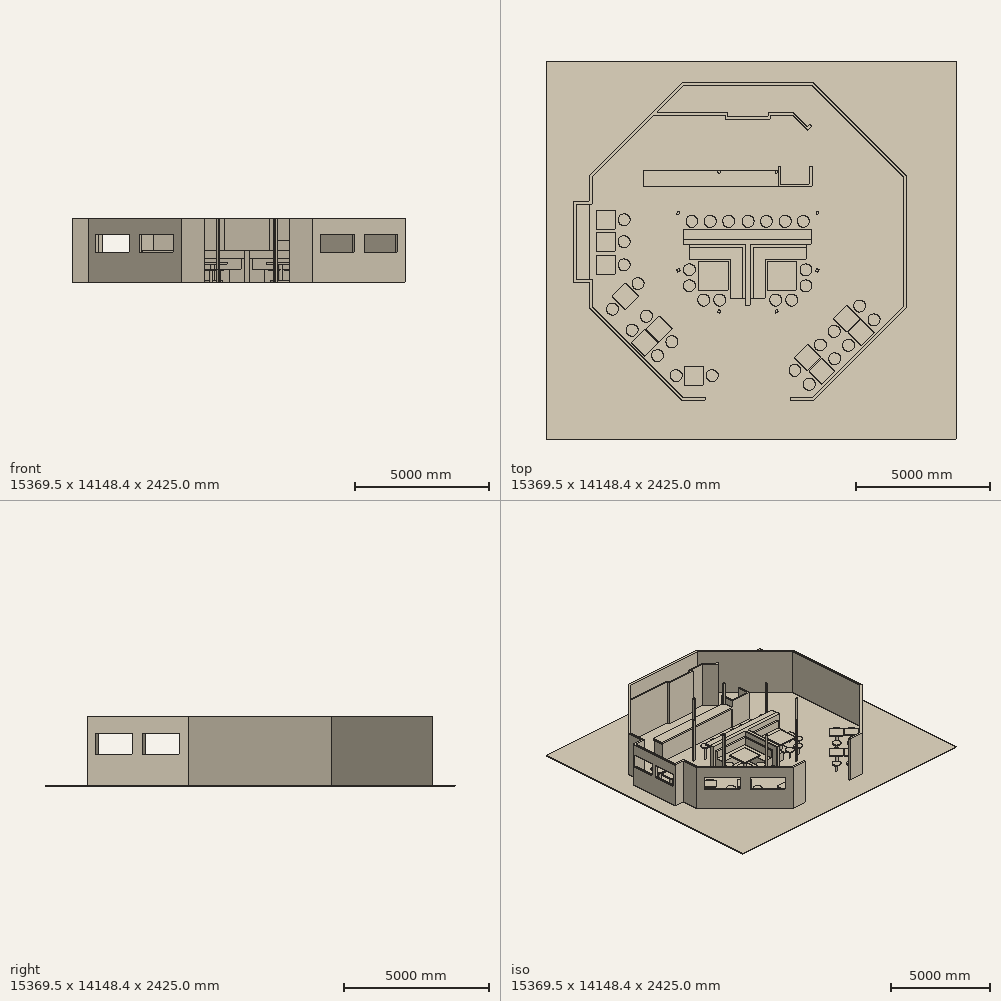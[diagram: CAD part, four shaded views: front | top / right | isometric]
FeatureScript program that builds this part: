
annotation { "Feature Type Name" : "Feature", "Feature Type Description" : "" }
export const myFeature = defineFeature(function(context is Context, id is Id, definition is map)
    precondition{}
    {
        {
            var Q0;
            Q0=qCreatedBy(makeId("Top.planeOp"),FACE);
            var sketch = newSketch(context, id + "F0", { "sketchPlane" : qUnion([Q0])});
            skLineSegment(sketch, "E0", {"start": v(-3956.26, -4309.82) * mm, "end": v(-4034.04, -4387.6) * mm});
            skLineSegment(sketch, "E1", {"start": v(-4309.82, -3956.26) * mm, "end": v(-4387.6, -4034.04) * mm});
            skLineSegment(sketch, "E2", {"start": v(-5582.6, -2683.47) * mm, "end": v(-5660.39, -2761.25) * mm});
            skLineSegment(sketch, "E3", {"start": v(-2683.47, -5582.6) * mm, "end": v(-2761.25, -5660.39) * mm});
            skLineSegment(sketch, "E4", {"start": v(-5845, -1400) * mm, "end": v(-6555, -1400) * mm});
            skLineSegment(sketch, "E5", {"start": v(-6445, 1400) * mm, "end": v(-6445, -1400) * mm});
            skLineSegment(sketch, "E6", {"start": v(-6555, 1510) * mm, "end": v(-6555, -1510) * mm});
            skLineSegment(sketch, "E7", {"start": v(-5955, -1510) * mm, "end": v(-6555, -1510) * mm});
            skLineSegment(sketch, "E8", {"start": v(-5845, 1400) * mm, "end": v(-6555, 1400) * mm});
            skLineSegment(sketch, "E9", {"start": v(-5955, 1510) * mm, "end": v(-6555, 1510) * mm});
            skLineSegment(sketch, "E10", {"start": v(-5845, -2421.08) * mm, "end": v(-2421.08, -5845) * mm});
            skLineSegment(sketch, "E11", {"start": v(-2421.08, -5845) * mm, "end": v(2421.08, -5845) * mm});
            skLineSegment(sketch, "E12", {"start": v(2421.08, -5845) * mm, "end": v(5845, -2421.08) * mm});
            skLineSegment(sketch, "E13", {"start": v(5845, -2421.08) * mm, "end": v(5845, 2421.08) * mm});
            skLineSegment(sketch, "E14", {"start": v(5845, 2421.08) * mm, "end": v(2421.08, 5845) * mm});
            skLineSegment(sketch, "E15", {"start": v(2421.08, 5845) * mm, "end": v(-2421.08, 5845) * mm});
            skLineSegment(sketch, "E16", {"start": v(-2421.08, 5845) * mm, "end": v(-3431.08, 4835) * mm});
            skLineSegment(sketch, "E17", {"start": v(-5845, 2421.08) * mm, "end": v(-5845, 1400) * mm});
            skLineSegment(sketch, "E18", {"start": v(-5955, -2466.64) * mm, "end": v(-2466.64, -5955) * mm});
            skLineSegment(sketch, "E19", {"start": v(-2466.64, -5955) * mm, "end": v(2466.64, -5955) * mm});
            skLineSegment(sketch, "E20", {"start": v(2466.64, -5955) * mm, "end": v(5955, -2466.64) * mm});
            skLineSegment(sketch, "E21", {"start": v(5955, -2466.64) * mm, "end": v(5955, 2466.64) * mm});
            skLineSegment(sketch, "E22", {"start": v(5955, 2466.64) * mm, "end": v(2466.64, 5955) * mm});
            skLineSegment(sketch, "E23", {"start": v(2466.64, 5955) * mm, "end": v(-2466.64, 5955) * mm});
            skLineSegment(sketch, "E24", {"start": v(-2466.64, 5955) * mm, "end": v(-5955, 2466.64) * mm});
            skLineSegment(sketch, "E25", {"start": v(-5955, 2466.64) * mm, "end": v(-5955, 1510) * mm});
            skLineSegment(sketch, "E26", {"start": v(-5845, -1400) * mm, "end": v(-5845, -2421.08) * mm});
            skLineSegment(sketch, "E27", {"start": v(-5955, -1510) * mm, "end": v(-5955, -2466.64) * mm});
            skLineSegment(sketch, "E28", {"start": v(4545, -1882.6) * mm, "end": v(4545, 1882.6) * mm});
            skLineSegment(sketch, "E29", {"start": v(4545, 1882.6) * mm, "end": v(3837.9, 2589.7) * mm});
            skLineSegment(sketch, "E30", {"start": v(4403.58, -2024.02) * mm, "end": v(4545, -1882.6) * mm});
            skLineSegment(sketch, "E31", {"start": v(5845, 2421.08) * mm, "end": v(4545, 1882.6) * mm});
            skLineSegment(sketch, "E32", {"start": v(5845, -2421.08) * mm, "end": v(4545, -1882.6) * mm});
            skLineSegment(sketch, "E33", {"start": v(4403.58, -2024.02) * mm, "end": v(5322.82, -2943.26) * mm});
            skLineSegment(sketch, "E34", {"start": v(3837.9, 2589.7) * mm, "end": v(4757.13, 3508.95) * mm});
            skLineSegment(sketch, "E35", {"start": v(-6445, -100) * mm, "end": v(-6555, -100) * mm});
            skLineSegment(sketch, "E36", {"start": v(-6445, 100) * mm, "end": v(-6555, 100) * mm});
            skLineSegment(sketch, "E37", {"start": v(-5955, 1400) * mm, "end": v(-5955, -1400) * mm});
            skLineSegment(sketch, "E38", {"start": v(-5845, 2421.08) * mm, "end": v(-5922.78, 2498.86) * mm});
            skLineSegment(sketch, "E39", {"start": v(-5420.74, 2845.34) * mm, "end": v(-5498.52, 2923.12) * mm});
            skLineSegment(sketch, "E40", {"start": v(-4147.94, 4118.13) * mm, "end": v(-4225.73, 4195.92) * mm});
            skLineSegment(sketch, "E41", {"start": v(3956.26, -4309.82) * mm, "end": v(4034.04, -4387.6) * mm});
            skLineSegment(sketch, "E42", {"start": v(4309.82, -3956.26) * mm, "end": v(4387.6, -4034.04) * mm});
            skLineSegment(sketch, "E43", {"start": v(5582.6, -2683.47) * mm, "end": v(5660.39, -2761.25) * mm});
            skLineSegment(sketch, "E44", {"start": v(2683.47, -5582.6) * mm, "end": v(2761.25, -5660.39) * mm});
            skLineSegment(sketch, "E45", {"start": v(3835, -1682.6) * mm, "end": v(3835, -1642.6) * mm});
            skLineSegment(sketch, "E46", {"start": v(3835, -1642.6) * mm, "end": v(4545, -1642.6) * mm});
            skLineSegment(sketch, "E47", {"start": v(4545, -1642.6) * mm, "end": v(4545, -1682.6) * mm});
            skLineSegment(sketch, "E48", {"start": v(4545, -1682.6) * mm, "end": v(3835, -1682.6) * mm});
            skLineSegment(sketch, "E49", {"start": v(2248.29, 4179.31) * mm, "end": v(1682.6, 4745) * mm});
            skLineSegment(sketch, "E50", {"start": v(-860, 4745) * mm, "end": v(-3521.08, 4745) * mm});
            skLineSegment(sketch, "E51", {"start": v(2248.29, 4306.6) * mm, "end": v(1719.88, 4835) * mm});
            skLineSegment(sketch, "E52", {"start": v(860, 4595) * mm, "end": v(-860, 4595) * mm});
            skLineSegment(sketch, "E53", {"start": v(860, 4745) * mm, "end": v(860, 4595) * mm});
            skLineSegment(sketch, "E54", {"start": v(-860, 4745) * mm, "end": v(-860, 4595) * mm});
            skLineSegment(sketch, "E55", {"start": v(1719.88, 4835) * mm, "end": v(770, 4835) * mm});
            skLineSegment(sketch, "E56", {"start": v(860, 4745) * mm, "end": v(1682.6, 4745) * mm});
            skLineSegment(sketch, "E57", {"start": v(770, 4835) * mm, "end": v(770, 4685) * mm});
            skLineSegment(sketch, "E58", {"start": v(-770, 4835) * mm, "end": v(-770, 4685) * mm});
            skLineSegment(sketch, "E59", {"start": v(770, 4685) * mm, "end": v(-770, 4685) * mm});
            skLineSegment(sketch, "E60", {"start": v(-770, 4835) * mm, "end": v(-3431.08, 4835) * mm});
            skLineSegment(sketch, "E61", {"start": v(-3521.08, 4745) * mm, "end": v(-5845, 2421.08) * mm});
            skLineSegment(sketch, "E62", {"start": v(0, -5845) * mm, "end": v(0, -5955) * mm});
            skLineSegment(sketch, "E63", {"start": v(1600, -5845) * mm, "end": v(1600, -5955) * mm});
            skLineSegment(sketch, "E64", {"start": v(-1600, -5845) * mm, "end": v(-1600, -5955) * mm});
            skLineSegment(sketch, "E65", {"start": v(-800, -5845) * mm, "end": v(-800, -5955) * mm});
            skLineSegment(sketch, "E66", {"start": v(800, -5845) * mm, "end": v(800, -5955) * mm});
            skLineSegment(sketch, "E67", {"start": v(-1570, -6755) * mm, "end": v(-1600, -6755) * mm});
            skLineSegment(sketch, "E68", {"start": v(-1600, -6755) * mm, "end": v(-1600, -5955) * mm});
            skLineSegment(sketch, "E69", {"start": v(-1600, -5955) * mm, "end": v(-1570, -5955) * mm});
            skLineSegment(sketch, "E70", {"start": v(-1570, -5955) * mm, "end": v(-1570, -6755) * mm});
            skLineSegment(sketch, "E71", {"start": v(1570, -6755) * mm, "end": v(1600, -6755) * mm});
            skLineSegment(sketch, "E72", {"start": v(1600, -6755) * mm, "end": v(1600, -5955) * mm});
            skLineSegment(sketch, "E73", {"start": v(1600, -5955) * mm, "end": v(1570, -5955) * mm});
            skLineSegment(sketch, "E74", {"start": v(1570, -5955) * mm, "end": v(1570, -6755) * mm});
            skLineSegment(sketch, "E75", {"start": v(-770, -6755) * mm, "end": v(-800, -6755) * mm});
            skLineSegment(sketch, "E76", {"start": v(-800, -6755) * mm, "end": v(-800, -5955) * mm});
            skLineSegment(sketch, "E77", {"start": v(-800, -5955) * mm, "end": v(-770, -5955) * mm});
            skLineSegment(sketch, "E78", {"start": v(-770, -5955) * mm, "end": v(-770, -6755) * mm});
            skLineSegment(sketch, "E79", {"start": v(770, -6755) * mm, "end": v(800, -6755) * mm});
            skLineSegment(sketch, "E80", {"start": v(800, -6755) * mm, "end": v(800, -5955) * mm});
            skLineSegment(sketch, "E81", {"start": v(800, -5955) * mm, "end": v(770, -5955) * mm});
            skLineSegment(sketch, "E82", {"start": v(770, -5955) * mm, "end": v(770, -6755) * mm});
            skArc(sketch, "E83", {"start": v(-1570, -6755) * mm, "mid": v(-1023.4, -6510.38) * mm, "end": v(-799.44, -5955) * mm});
            skLineSegment(sketch, "E84", {"start": v(-800, -5955) * mm, "end": v(0, -5955) * mm});
            skLineSegment(sketch, "E85", {"start": v(0, -5955) * mm, "end": v(-800, -5955) * mm});
            skArc(sketch, "E86", {"start": v(-800, -6755) * mm, "mid": v(-234.31, -6520.69) * mm, "end": v(0, -5955) * mm});
            skArc(sketch, "E87", {"start": v(799.44, -5955) * mm, "mid": v(1023.4, -6510.38) * mm, "end": v(1570, -6755) * mm});
            skArc(sketch, "E88", {"start": v(0, -5955) * mm, "mid": v(234.31, -6520.69) * mm, "end": v(800, -6755) * mm});
            skArc(sketch, "E89", {"start": v(4545, -971.47) * mm, "mid": v(4056.5, -1165.81) * mm, "end": v(3835, -1642.6) * mm});
            skLineSegment(sketch, "E90", {"start": v(2248.29, 4179.31) * mm, "end": v(2389.7, 4320.74) * mm});
            skLineSegment(sketch, "E91", {"start": v(2248.29, 4306.6) * mm, "end": v(2326.07, 4384.38) * mm});
            skLineSegment(sketch, "E92", {"start": v(2326.07, 4384.38) * mm, "end": v(2389.7, 4320.74) * mm});
            skLineSegment(sketch, "E93", {"start": v(-2421.08, 5845) * mm, "end": v(-2466.64, 5955) * mm});
            skLineSegment(sketch, "E94", {"start": v(5845, 2421.08) * mm, "end": v(5955, 2466.64) * mm});
            skLineSegment(sketch, "E95", {"start": v(4246.23, -3897.34) * mm, "end": v(3758.32, -3409.44) * mm});
            skArc(sketch, "E96", {"start": v(3758.32, -3409.44) * mm, "mid": v(3756.86, -3405.9) * mm, "end": v(3758.32, -3402.37) * mm});
            skLineSegment(sketch, "E97", {"start": v(3758.32, -3402.37) * mm, "end": v(4246.23, -2914.47) * mm});
            skArc(sketch, "E98", {"start": v(4246.23, -2914.47) * mm, "mid": v(4249.76, -2913) * mm, "end": v(4253.3, -2914.47) * mm});
            skLineSegment(sketch, "E99", {"start": v(4253.3, -2914.47) * mm, "end": v(4741.2, -3402.37) * mm});
            skArc(sketch, "E100", {"start": v(4741.2, -3402.37) * mm, "mid": v(4742.67, -3405.9) * mm, "end": v(4741.2, -3409.44) * mm});
            skLineSegment(sketch, "E101", {"start": v(4741.2, -3409.44) * mm, "end": v(4253.3, -3897.34) * mm});
            skArc(sketch, "E102", {"start": v(4253.3, -3897.34) * mm, "mid": v(4249.76, -3898.8) * mm, "end": v(4246.23, -3897.34) * mm});
            skCircle(sketch, "E103", {"center": v(3772.46, -3883.2) * mm, "radius": 225 * mm});
            skCircle(sketch, "E104", {"center": v(4727.06, -2928.6) * mm, "radius": 225 * mm});
            skLineSegment(sketch, "E105", {"start": v(3708.26, -3376.45) * mm, "end": v(3220.35, -2888.55) * mm});
            skArc(sketch, "E106", {"start": v(3220.35, -2888.55) * mm, "mid": v(3218.89, -2885.01) * mm, "end": v(3220.35, -2881.48) * mm});
            skLineSegment(sketch, "E107", {"start": v(3220.35, -2881.48) * mm, "end": v(3708.26, -2393.58) * mm});
            skArc(sketch, "E108", {"start": v(3708.26, -2393.58) * mm, "mid": v(3711.8, -2392.11) * mm, "end": v(3715.33, -2393.58) * mm});
            skLineSegment(sketch, "E109", {"start": v(3715.33, -2393.58) * mm, "end": v(4203.23, -2881.48) * mm});
            skArc(sketch, "E110", {"start": v(4203.23, -2881.48) * mm, "mid": v(4204.7, -2885.01) * mm, "end": v(4203.23, -2888.55) * mm});
            skLineSegment(sketch, "E111", {"start": v(4203.23, -2888.55) * mm, "end": v(3715.33, -3376.45) * mm});
            skArc(sketch, "E112", {"start": v(3715.33, -3376.45) * mm, "mid": v(3711.8, -3377.92) * mm, "end": v(3708.26, -3376.45) * mm});
            skCircle(sketch, "E113", {"center": v(3234.5, -3362.31) * mm, "radius": 225 * mm});
            skCircle(sketch, "E114", {"center": v(4189.09, -2407.72) * mm, "radius": 225 * mm});
            skLineSegment(sketch, "E115", {"start": v(-3861.24, -4284.67) * mm, "end": v(-3373.34, -3796.76) * mm});
            skArc(sketch, "E116", {"start": v(-3373.34, -3796.76) * mm, "mid": v(-3371.87, -3793.23) * mm, "end": v(-3373.34, -3789.7) * mm});
            skLineSegment(sketch, "E117", {"start": v(-3373.34, -3789.7) * mm, "end": v(-3861.24, -3301.79) * mm});
            skArc(sketch, "E118", {"start": v(-3861.24, -3301.79) * mm, "mid": v(-3864.78, -3300.33) * mm, "end": v(-3868.31, -3301.79) * mm});
            skLineSegment(sketch, "E119", {"start": v(-3868.31, -3301.79) * mm, "end": v(-4356.22, -3789.7) * mm});
            skArc(sketch, "E120", {"start": v(-4356.22, -3789.7) * mm, "mid": v(-4357.68, -3793.23) * mm, "end": v(-4356.22, -3796.76) * mm});
            skLineSegment(sketch, "E121", {"start": v(-4356.22, -3796.76) * mm, "end": v(-3868.31, -4284.67) * mm});
            skArc(sketch, "E122", {"start": v(-3868.31, -4284.67) * mm, "mid": v(-3864.78, -4286.13) * mm, "end": v(-3861.24, -4284.67) * mm});
            skCircle(sketch, "E123", {"center": v(-3387.48, -4270.53) * mm, "radius": 225 * mm});
            skCircle(sketch, "E124", {"center": v(-4342.08, -3315.93) * mm, "radius": 225 * mm});
            skLineSegment(sketch, "E125", {"start": v(-3323.27, -3763.78) * mm, "end": v(-2835.37, -3275.87) * mm});
            skArc(sketch, "E126", {"start": v(-2835.37, -3275.87) * mm, "mid": v(-2833.9, -3272.34) * mm, "end": v(-2835.37, -3268.8) * mm});
            skLineSegment(sketch, "E127", {"start": v(-2835.37, -3268.8) * mm, "end": v(-3323.27, -2780.9) * mm});
            skArc(sketch, "E128", {"start": v(-3323.27, -2780.9) * mm, "mid": v(-3326.8, -2779.43) * mm, "end": v(-3330.34, -2780.9) * mm});
            skLineSegment(sketch, "E129", {"start": v(-3330.34, -2780.9) * mm, "end": v(-3818.25, -3268.8) * mm});
            skArc(sketch, "E130", {"start": v(-3818.25, -3268.8) * mm, "mid": v(-3819.71, -3272.34) * mm, "end": v(-3818.25, -3275.87) * mm});
            skLineSegment(sketch, "E131", {"start": v(-3818.25, -3275.87) * mm, "end": v(-3330.34, -3763.78) * mm});
            skArc(sketch, "E132", {"start": v(-3330.34, -3763.78) * mm, "mid": v(-3326.8, -3765.24) * mm, "end": v(-3323.27, -3763.78) * mm});
            skCircle(sketch, "E133", {"center": v(-2849.51, -3749.64) * mm, "radius": 225 * mm});
            skCircle(sketch, "E134", {"center": v(-3804.1, -2795.04) * mm, "radius": 225 * mm});
            skLineSegment(sketch, "E135", {"start": v(-5663.66, -522.26) * mm, "end": v(-5663.66, -1212.26) * mm});
            skArc(sketch, "E136", {"start": v(-5663.66, -1212.26) * mm, "mid": v(-5662.2, -1215.8) * mm, "end": v(-5658.66, -1217.26) * mm});
            skLineSegment(sketch, "E137", {"start": v(-5658.66, -1217.26) * mm, "end": v(-4968.66, -1217.26) * mm});
            skArc(sketch, "E138", {"start": v(-4968.66, -1217.26) * mm, "mid": v(-4965.12, -1215.8) * mm, "end": v(-4963.66, -1212.26) * mm});
            skLineSegment(sketch, "E139", {"start": v(-4963.66, -1212.26) * mm, "end": v(-4963.66, -522.26) * mm});
            skArc(sketch, "E140", {"start": v(-4963.66, -522.26) * mm, "mid": v(-4965.12, -518.73) * mm, "end": v(-4968.66, -517.26) * mm});
            skLineSegment(sketch, "E141", {"start": v(-4968.66, -517.26) * mm, "end": v(-5658.66, -517.26) * mm});
            skArc(sketch, "E142", {"start": v(-5658.66, -517.26) * mm, "mid": v(-5662.2, -518.73) * mm, "end": v(-5663.66, -522.26) * mm});
            skCircle(sketch, "E143", {"center": v(-4638.66, -867.26) * mm, "radius": 225 * mm});
            skLineSegment(sketch, "E144", {"start": v(-5089.1, -2050.87) * mm, "end": v(-4601.2, -2538.77) * mm});
            skArc(sketch, "E145", {"start": v(-4601.2, -2538.77) * mm, "mid": v(-4597.67, -2540.24) * mm, "end": v(-4594.13, -2538.77) * mm});
            skLineSegment(sketch, "E146", {"start": v(-4594.13, -2538.77) * mm, "end": v(-4106.23, -2050.87) * mm});
            skArc(sketch, "E147", {"start": v(-4106.23, -2050.87) * mm, "mid": v(-4104.77, -2047.33) * mm, "end": v(-4106.23, -2043.8) * mm});
            skLineSegment(sketch, "E148", {"start": v(-4106.23, -2043.8) * mm, "end": v(-4594.13, -1555.9) * mm});
            skArc(sketch, "E149", {"start": v(-4594.13, -1555.9) * mm, "mid": v(-4597.67, -1554.43) * mm, "end": v(-4601.2, -1555.9) * mm});
            skLineSegment(sketch, "E150", {"start": v(-4601.2, -1555.9) * mm, "end": v(-5089.1, -2043.8) * mm});
            skArc(sketch, "E151", {"start": v(-5089.1, -2043.8) * mm, "mid": v(-5090.57, -2047.33) * mm, "end": v(-5089.1, -2050.87) * mm});
            skCircle(sketch, "E152", {"center": v(-5074.97, -2524.63) * mm, "radius": 225 * mm});
            skCircle(sketch, "E153", {"center": v(-4120.37, -1570.04) * mm, "radius": 225 * mm});
            skLineSegment(sketch, "E154", {"start": v(-5663.66, 345) * mm, "end": v(-5663.66, -345) * mm});
            skArc(sketch, "E155", {"start": v(-5663.66, -345) * mm, "mid": v(-5662.2, -348.54) * mm, "end": v(-5658.66, -350) * mm});
            skLineSegment(sketch, "E156", {"start": v(-5658.66, -350) * mm, "end": v(-4968.66, -350) * mm});
            skArc(sketch, "E157", {"start": v(-4968.66, -350) * mm, "mid": v(-4965.12, -348.54) * mm, "end": v(-4963.66, -345) * mm});
            skLineSegment(sketch, "E158", {"start": v(-4963.66, -345) * mm, "end": v(-4963.66, 345) * mm});
            skArc(sketch, "E159", {"start": v(-4963.66, 345) * mm, "mid": v(-4965.12, 348.54) * mm, "end": v(-4968.66, 350) * mm});
            skLineSegment(sketch, "E160", {"start": v(-4968.66, 350) * mm, "end": v(-5658.66, 350) * mm});
            skArc(sketch, "E161", {"start": v(-5658.66, 350) * mm, "mid": v(-5662.2, 348.54) * mm, "end": v(-5663.66, 345) * mm});
            skCircle(sketch, "E162", {"center": v(-4638.66, 0) * mm, "radius": 225 * mm});
            skLineSegment(sketch, "E163", {"start": v(-5663.66, 1167.79) * mm, "end": v(-5663.66, 477.79) * mm});
            skArc(sketch, "E164", {"start": v(-5663.66, 477.79) * mm, "mid": v(-5662.2, 474.25) * mm, "end": v(-5658.66, 472.79) * mm});
            skLineSegment(sketch, "E165", {"start": v(-5658.66, 472.79) * mm, "end": v(-4968.66, 472.79) * mm});
            skArc(sketch, "E166", {"start": v(-4968.66, 472.79) * mm, "mid": v(-4965.12, 474.25) * mm, "end": v(-4963.66, 477.79) * mm});
            skLineSegment(sketch, "E167", {"start": v(-4963.66, 477.79) * mm, "end": v(-4963.66, 1167.79) * mm});
            skArc(sketch, "E168", {"start": v(-4963.66, 1167.79) * mm, "mid": v(-4965.12, 1171.32) * mm, "end": v(-4968.66, 1172.79) * mm});
            skLineSegment(sketch, "E169", {"start": v(-4968.66, 1172.79) * mm, "end": v(-5658.66, 1172.79) * mm});
            skArc(sketch, "E170", {"start": v(-5658.66, 1172.79) * mm, "mid": v(-5662.2, 1171.32) * mm, "end": v(-5663.66, 1167.79) * mm});
            skCircle(sketch, "E171", {"center": v(-4638.66, 822.79) * mm, "radius": 225 * mm});
            skLineSegment(sketch, "E172", {"start": v(-2408.95, -103.03) * mm, "end": v(-2408.95, 96.97) * mm});
            skLineSegment(sketch, "E173", {"start": v(-2408.95, 96.97) * mm, "end": v(2391.05, 96.97) * mm});
            skLineSegment(sketch, "E174", {"start": v(2391.05, 96.97) * mm, "end": v(2391.05, -103.03) * mm});
            skLineSegment(sketch, "E175", {"start": v(2391.05, -103.03) * mm, "end": v(-2408.95, -103.03) * mm});
            skLineSegment(sketch, "E176", {"start": v(91.05, -2112.15) * mm, "end": v(91.05, -103.03) * mm});
            skLineSegment(sketch, "E177", {"start": v(191.05, -203.03) * mm, "end": v(191.05, -2112.15) * mm});
            skLineSegment(sketch, "E178", {"start": v(191.05, -2112.15) * mm, "end": v(91.05, -2112.15) * mm});
            skLineSegment(sketch, "E179", {"start": v(2191.06, -203.03) * mm, "end": v(191.05, -203.03) * mm});
            skLineSegment(sketch, "E180", {"start": v(91.05, -103.03) * mm, "end": v(2191.06, -103.03) * mm});
            skLineSegment(sketch, "E181", {"start": v(2191.06, -103.03) * mm, "end": v(2191.06, -203.03) * mm});
            skLineSegment(sketch, "E182", {"start": v(191.05, -2112.15) * mm, "end": v(191.05, -203.03) * mm});
            skLineSegment(sketch, "E183", {"start": v(191.05, -203.03) * mm, "end": v(2191.06, -203.03) * mm});
            skLineSegment(sketch, "E184", {"start": v(-2362.95, -5365.31) * mm, "end": v(-2362.95, -4675.31) * mm});
            skArc(sketch, "E185", {"start": v(-2362.95, -4675.31) * mm, "mid": v(-2361.48, -4671.78) * mm, "end": v(-2357.95, -4670.31) * mm});
            skLineSegment(sketch, "E186", {"start": v(-2357.95, -4670.31) * mm, "end": v(-1667.95, -4670.31) * mm});
            skArc(sketch, "E187", {"start": v(-1667.95, -4670.31) * mm, "mid": v(-1664.41, -4671.78) * mm, "end": v(-1662.95, -4675.31) * mm});
            skLineSegment(sketch, "E188", {"start": v(-1662.95, -4675.31) * mm, "end": v(-1662.95, -5365.31) * mm});
            skArc(sketch, "E189", {"start": v(-1662.95, -5365.31) * mm, "mid": v(-1664.41, -5368.85) * mm, "end": v(-1667.95, -5370.31) * mm});
            skLineSegment(sketch, "E190", {"start": v(-1667.95, -5370.31) * mm, "end": v(-2357.95, -5370.31) * mm});
            skArc(sketch, "E191", {"start": v(-2357.95, -5370.31) * mm, "mid": v(-2361.48, -5368.85) * mm, "end": v(-2362.95, -5365.31) * mm});
            skCircle(sketch, "E192", {"center": v(-2687.95, -5020.31) * mm, "radius": 225 * mm});
            skCircle(sketch, "E193", {"center": v(-1337.95, -5020.31) * mm, "radius": 225 * mm});
            skCircle(sketch, "E194", {"center": v(-5988.66, -867.26) * mm, "radius": 125 * mm});
            skCircle(sketch, "E195", {"center": v(-5988.66, 0) * mm, "radius": 125 * mm});
            skCircle(sketch, "E196", {"center": v(-5988.66, 822.79) * mm, "radius": 125 * mm});
            skLineSegment(sketch, "E197", {"start": v(-108.95, -2112.15) * mm, "end": v(-108.95, -103.03) * mm});
            skLineSegment(sketch, "E198", {"start": v(-208.95, -203.03) * mm, "end": v(-208.95, -2112.15) * mm});
            skLineSegment(sketch, "E199", {"start": v(-208.95, -2112.15) * mm, "end": v(-108.95, -2112.15) * mm});
            skLineSegment(sketch, "E200", {"start": v(-2208.97, -203.03) * mm, "end": v(-208.95, -203.03) * mm});
            skLineSegment(sketch, "E201", {"start": v(-108.95, -103.03) * mm, "end": v(-2208.97, -103.03) * mm});
            skLineSegment(sketch, "E202", {"start": v(-2208.97, -103.03) * mm, "end": v(-2208.97, -203.03) * mm});
            skLineSegment(sketch, "E203", {"start": v(-208.95, -2112.15) * mm, "end": v(-208.95, -203.03) * mm});
            skLineSegment(sketch, "E204", {"start": v(-658.95, -653.03) * mm, "end": v(-658.95, -2112.15) * mm});
            skLineSegment(sketch, "E205", {"start": v(-658.95, -2112.15) * mm, "end": v(-208.95, -2112.15) * mm});
            skLineSegment(sketch, "E206", {"start": v(-208.95, -203.03) * mm, "end": v(-2208.97, -203.03) * mm});
            skLineSegment(sketch, "E207", {"start": v(-2208.97, -203.03) * mm, "end": v(-2208.97, -653.03) * mm});
            skLineSegment(sketch, "E208", {"start": v(-2208.97, -653.03) * mm, "end": v(-658.95, -653.03) * mm});
            skCircle(sketch, "E209", {"center": v(-2192.43, -1653.03) * mm, "radius": 225 * mm});
            skCircle(sketch, "E210", {"center": v(-1658.95, -410.86) * mm, "radius": 125 * mm});
            skCircle(sketch, "E211", {"center": v(-1058.95, -414.5) * mm, "radius": 125 * mm});
            skLineSegment(sketch, "E212", {"start": v(-108.95, 96.97) * mm, "end": v(-2306.97, 96.97) * mm});
            skLineSegment(sketch, "E213", {"start": v(91.05, 96.97) * mm, "end": v(2289.06, 96.97) * mm});
            skLineSegment(sketch, "E214", {"start": v(2773.22, -5356.12) * mm, "end": v(2285.31, -4868.22) * mm});
            skArc(sketch, "E215", {"start": v(2285.31, -4868.22) * mm, "mid": v(2283.85, -4864.68) * mm, "end": v(2285.31, -4861.15) * mm});
            skLineSegment(sketch, "E216", {"start": v(2285.31, -4861.15) * mm, "end": v(2773.22, -4373.24) * mm});
            skArc(sketch, "E217", {"start": v(2773.22, -4373.24) * mm, "mid": v(2776.75, -4371.78) * mm, "end": v(2780.29, -4373.24) * mm});
            skLineSegment(sketch, "E218", {"start": v(2780.29, -4373.24) * mm, "end": v(3268.2, -4861.15) * mm});
            skArc(sketch, "E219", {"start": v(3268.2, -4861.15) * mm, "mid": v(3269.66, -4864.68) * mm, "end": v(3268.2, -4868.22) * mm});
            skLineSegment(sketch, "E220", {"start": v(3268.2, -4868.22) * mm, "end": v(2780.29, -5356.12) * mm});
            skArc(sketch, "E221", {"start": v(2780.29, -5356.12) * mm, "mid": v(2776.75, -5357.59) * mm, "end": v(2773.22, -5356.12) * mm});
            skCircle(sketch, "E222", {"center": v(2299.45, -5341.98) * mm, "radius": 225 * mm});
            skCircle(sketch, "E223", {"center": v(3254.05, -4387.39) * mm, "radius": 225 * mm});
            skLineSegment(sketch, "E224", {"start": v(2235.25, -4835.23) * mm, "end": v(1747.34, -4347.33) * mm});
            skArc(sketch, "E225", {"start": v(1747.34, -4347.33) * mm, "mid": v(1745.88, -4343.8) * mm, "end": v(1747.34, -4340.26) * mm});
            skLineSegment(sketch, "E226", {"start": v(1747.34, -4340.26) * mm, "end": v(2235.25, -3852.35) * mm});
            skArc(sketch, "E227", {"start": v(2235.25, -3852.35) * mm, "mid": v(2238.78, -3850.89) * mm, "end": v(2242.32, -3852.35) * mm});
            skLineSegment(sketch, "E228", {"start": v(2242.32, -3852.35) * mm, "end": v(2730.22, -4340.26) * mm});
            skArc(sketch, "E229", {"start": v(2730.22, -4340.26) * mm, "mid": v(2731.69, -4343.8) * mm, "end": v(2730.22, -4347.33) * mm});
            skLineSegment(sketch, "E230", {"start": v(2730.22, -4347.33) * mm, "end": v(2242.32, -4835.23) * mm});
            skArc(sketch, "E231", {"start": v(2242.32, -4835.23) * mm, "mid": v(2238.78, -4836.7) * mm, "end": v(2235.25, -4835.23) * mm});
            skCircle(sketch, "E232", {"center": v(1761.49, -4821.09) * mm, "radius": 225 * mm});
            skCircle(sketch, "E233", {"center": v(2716.08, -3866.5) * mm, "radius": 225 * mm});
            skLineSegment(sketch, "E234", {"start": v(-1840.95, -1830.03) * mm, "end": v(-1840.95, -738.03) * mm});
            skArc(sketch, "E235", {"start": v(-1840.95, -738.03) * mm, "mid": v(-1839.49, -734.5) * mm, "end": v(-1835.95, -733.03) * mm});
            skLineSegment(sketch, "E236", {"start": v(-1835.95, -733.03) * mm, "end": v(-743.95, -733.03) * mm});
            skArc(sketch, "E237", {"start": v(-743.95, -733.03) * mm, "mid": v(-740.42, -734.5) * mm, "end": v(-738.95, -738.03) * mm});
            skLineSegment(sketch, "E238", {"start": v(-738.95, -738.03) * mm, "end": v(-738.95, -1830.03) * mm});
            skArc(sketch, "E239", {"start": v(-738.95, -1830.03) * mm, "mid": v(-740.42, -1833.56) * mm, "end": v(-743.95, -1835.03) * mm});
            skLineSegment(sketch, "E240", {"start": v(-743.95, -1835.03) * mm, "end": v(-1835.95, -1835.03) * mm});
            skArc(sketch, "E241", {"start": v(-1835.95, -1835.03) * mm, "mid": v(-1839.49, -1833.56) * mm, "end": v(-1840.95, -1830.03) * mm});
            skCircle(sketch, "E242", {"center": v(-2192.43, -1053.03) * mm, "radius": 225 * mm});
            skCircle(sketch, "E243", {"center": v(-1658.95, -2186.5) * mm, "radius": 225 * mm});
            skCircle(sketch, "E244", {"center": v(-1058.95, -2186.5) * mm, "radius": 225 * mm});
            skCircle(sketch, "E245", {"center": v(-416.78, -1653.03) * mm, "radius": 125 * mm});
            skCircle(sketch, "E246", {"center": v(-420.43, -1053.03) * mm, "radius": 125 * mm});
            skLineSegment(sketch, "E247", {"start": v(-1104.68, 2546.22) * mm, "end": v(-1140.65, 2633.07) * mm});
            skArc(sketch, "E248", {"start": v(-1140.65, 2633.07) * mm, "mid": v(-1140.65, 2635.36) * mm, "end": v(-1139.03, 2636.99) * mm});
            skLineSegment(sketch, "E249", {"start": v(-1139.03, 2636.99) * mm, "end": v(-1052.18, 2672.96) * mm});
            skArc(sketch, "E250", {"start": v(-1052.18, 2672.96) * mm, "mid": v(-1049.89, 2672.96) * mm, "end": v(-1048.26, 2671.34) * mm});
            skLineSegment(sketch, "E251", {"start": v(-1048.26, 2671.34) * mm, "end": v(-1012.3, 2584.5) * mm});
            skArc(sketch, "E252", {"start": v(-1012.3, 2584.5) * mm, "mid": v(-1012.3, 2582.2) * mm, "end": v(-1013.92, 2580.57) * mm});
            skLineSegment(sketch, "E253", {"start": v(-1013.92, 2580.57) * mm, "end": v(-1100.76, 2544.6) * mm});
            skArc(sketch, "E254", {"start": v(-1100.76, 2544.6) * mm, "mid": v(-1103.06, 2544.6) * mm, "end": v(-1104.68, 2546.22) * mm});
            skLineSegment(sketch, "E255", {"start": v(1104.68, 2546.22) * mm, "end": v(1140.65, 2633.07) * mm});
            skArc(sketch, "E256", {"start": v(1140.65, 2633.07) * mm, "mid": v(1140.65, 2635.36) * mm, "end": v(1139.03, 2636.99) * mm});
            skLineSegment(sketch, "E257", {"start": v(1139.03, 2636.99) * mm, "end": v(1052.18, 2672.96) * mm});
            skArc(sketch, "E258", {"start": v(1052.18, 2672.96) * mm, "mid": v(1049.89, 2672.96) * mm, "end": v(1048.26, 2671.34) * mm});
            skLineSegment(sketch, "E259", {"start": v(1048.26, 2671.34) * mm, "end": v(1012.3, 2584.5) * mm});
            skArc(sketch, "E260", {"start": v(1012.3, 2584.5) * mm, "mid": v(1012.3, 2582.2) * mm, "end": v(1013.92, 2580.57) * mm});
            skLineSegment(sketch, "E261", {"start": v(1013.92, 2580.57) * mm, "end": v(1100.76, 2544.6) * mm});
            skArc(sketch, "E262", {"start": v(1100.76, 2544.6) * mm, "mid": v(1103.06, 2544.6) * mm, "end": v(1104.68, 2546.22) * mm});
            skLineSegment(sketch, "E263", {"start": v(1104.68, -2546.22) * mm, "end": v(1140.65, -2633.07) * mm});
            skArc(sketch, "E264", {"start": v(1140.65, -2633.07) * mm, "mid": v(1140.65, -2635.36) * mm, "end": v(1139.03, -2636.99) * mm});
            skLineSegment(sketch, "E265", {"start": v(1139.03, -2636.99) * mm, "end": v(1052.18, -2672.96) * mm});
            skArc(sketch, "E266", {"start": v(1052.18, -2672.96) * mm, "mid": v(1049.89, -2672.96) * mm, "end": v(1048.26, -2671.34) * mm});
            skLineSegment(sketch, "E267", {"start": v(1048.26, -2671.34) * mm, "end": v(1012.3, -2584.5) * mm});
            skArc(sketch, "E268", {"start": v(1012.3, -2584.5) * mm, "mid": v(1012.3, -2582.2) * mm, "end": v(1013.92, -2580.57) * mm});
            skLineSegment(sketch, "E269", {"start": v(1013.92, -2580.57) * mm, "end": v(1100.76, -2544.6) * mm});
            skArc(sketch, "E270", {"start": v(1100.76, -2544.6) * mm, "mid": v(1103.06, -2544.6) * mm, "end": v(1104.68, -2546.22) * mm});
            skLineSegment(sketch, "E271", {"start": v(-1104.68, -2546.22) * mm, "end": v(-1140.65, -2633.07) * mm});
            skArc(sketch, "E272", {"start": v(-1140.65, -2633.07) * mm, "mid": v(-1140.65, -2635.36) * mm, "end": v(-1139.03, -2636.99) * mm});
            skLineSegment(sketch, "E273", {"start": v(-1139.03, -2636.99) * mm, "end": v(-1052.18, -2672.96) * mm});
            skArc(sketch, "E274", {"start": v(-1052.18, -2672.96) * mm, "mid": v(-1049.89, -2672.96) * mm, "end": v(-1048.26, -2671.34) * mm});
            skLineSegment(sketch, "E275", {"start": v(-1048.26, -2671.34) * mm, "end": v(-1012.3, -2584.5) * mm});
            skArc(sketch, "E276", {"start": v(-1012.3, -2584.5) * mm, "mid": v(-1012.3, -2582.2) * mm, "end": v(-1013.92, -2580.57) * mm});
            skLineSegment(sketch, "E277", {"start": v(-1013.92, -2580.57) * mm, "end": v(-1100.76, -2544.6) * mm});
            skArc(sketch, "E278", {"start": v(-1100.76, -2544.6) * mm, "mid": v(-1103.06, -2544.6) * mm, "end": v(-1104.68, -2546.22) * mm});
            skLineSegment(sketch, "E279", {"start": v(-2546.22, 1104.68) * mm, "end": v(-2633.07, 1140.65) * mm});
            skArc(sketch, "E280", {"start": v(-2633.07, 1140.65) * mm, "mid": v(-2635.36, 1140.65) * mm, "end": v(-2636.99, 1139.03) * mm});
            skLineSegment(sketch, "E281", {"start": v(-2636.99, 1139.03) * mm, "end": v(-2672.96, 1052.18) * mm});
            skArc(sketch, "E282", {"start": v(-2672.96, 1052.18) * mm, "mid": v(-2672.96, 1049.89) * mm, "end": v(-2671.34, 1048.26) * mm});
            skLineSegment(sketch, "E283", {"start": v(-2671.34, 1048.26) * mm, "end": v(-2584.5, 1012.3) * mm});
            skArc(sketch, "E284", {"start": v(-2584.5, 1012.3) * mm, "mid": v(-2582.2, 1012.3) * mm, "end": v(-2580.57, 1013.92) * mm});
            skLineSegment(sketch, "E285", {"start": v(-2580.57, 1013.92) * mm, "end": v(-2544.6, 1100.76) * mm});
            skArc(sketch, "E286", {"start": v(-2544.6, 1100.76) * mm, "mid": v(-2544.6, 1103.06) * mm, "end": v(-2546.22, 1104.68) * mm});
            skLineSegment(sketch, "E287", {"start": v(-2546.22, -1104.68) * mm, "end": v(-2633.07, -1140.65) * mm});
            skArc(sketch, "E288", {"start": v(-2633.07, -1140.65) * mm, "mid": v(-2635.36, -1140.65) * mm, "end": v(-2636.99, -1139.03) * mm});
            skLineSegment(sketch, "E289", {"start": v(-2636.99, -1139.03) * mm, "end": v(-2672.96, -1052.18) * mm});
            skArc(sketch, "E290", {"start": v(-2672.96, -1052.18) * mm, "mid": v(-2672.96, -1049.89) * mm, "end": v(-2671.34, -1048.26) * mm});
            skLineSegment(sketch, "E291", {"start": v(-2671.34, -1048.26) * mm, "end": v(-2584.5, -1012.3) * mm});
            skArc(sketch, "E292", {"start": v(-2584.5, -1012.3) * mm, "mid": v(-2582.2, -1012.3) * mm, "end": v(-2580.57, -1013.92) * mm});
            skLineSegment(sketch, "E293", {"start": v(-2580.57, -1013.92) * mm, "end": v(-2544.6, -1100.76) * mm});
            skArc(sketch, "E294", {"start": v(-2544.6, -1100.76) * mm, "mid": v(-2544.6, -1103.06) * mm, "end": v(-2546.22, -1104.68) * mm});
            skLineSegment(sketch, "E295", {"start": v(2546.22, -1104.68) * mm, "end": v(2633.07, -1140.65) * mm});
            skArc(sketch, "E296", {"start": v(2633.07, -1140.65) * mm, "mid": v(2635.36, -1140.65) * mm, "end": v(2636.99, -1139.03) * mm});
            skLineSegment(sketch, "E297", {"start": v(2636.99, -1139.03) * mm, "end": v(2672.96, -1052.18) * mm});
            skArc(sketch, "E298", {"start": v(2672.96, -1052.18) * mm, "mid": v(2672.96, -1049.89) * mm, "end": v(2671.34, -1048.26) * mm});
            skLineSegment(sketch, "E299", {"start": v(2671.34, -1048.26) * mm, "end": v(2584.5, -1012.3) * mm});
            skArc(sketch, "E300", {"start": v(2584.5, -1012.3) * mm, "mid": v(2582.2, -1012.3) * mm, "end": v(2580.57, -1013.92) * mm});
            skLineSegment(sketch, "E301", {"start": v(2580.57, -1013.92) * mm, "end": v(2544.6, -1100.76) * mm});
            skArc(sketch, "E302", {"start": v(2544.6, -1100.76) * mm, "mid": v(2544.6, -1103.06) * mm, "end": v(2546.22, -1104.68) * mm});
            skLineSegment(sketch, "E303", {"start": v(2546.22, 1104.68) * mm, "end": v(2633.07, 1140.65) * mm});
            skArc(sketch, "E304", {"start": v(2633.07, 1140.65) * mm, "mid": v(2635.36, 1140.65) * mm, "end": v(2636.99, 1139.03) * mm});
            skLineSegment(sketch, "E305", {"start": v(2636.99, 1139.03) * mm, "end": v(2672.96, 1052.18) * mm});
            skArc(sketch, "E306", {"start": v(2672.96, 1052.18) * mm, "mid": v(2672.96, 1049.89) * mm, "end": v(2671.34, 1048.26) * mm});
            skLineSegment(sketch, "E307", {"start": v(2671.34, 1048.26) * mm, "end": v(2584.5, 1012.3) * mm});
            skArc(sketch, "E308", {"start": v(2584.5, 1012.3) * mm, "mid": v(2582.2, 1012.3) * mm, "end": v(2580.57, 1013.92) * mm});
            skLineSegment(sketch, "E309", {"start": v(2580.57, 1013.92) * mm, "end": v(2544.6, 1100.76) * mm});
            skArc(sketch, "E310", {"start": v(2544.6, 1100.76) * mm, "mid": v(2544.6, 1103.06) * mm, "end": v(2546.22, 1104.68) * mm});
            skLineSegment(sketch, "E311", {"start": v(-3905, 2073.45) * mm, "end": v(1154.25, 2073.45) * mm});
            skLineSegment(sketch, "E312", {"start": v(1154.25, 2073.45) * mm, "end": v(1154.25, 2673.45) * mm});
            skLineSegment(sketch, "E313", {"start": v(91.05, 96.97) * mm, "end": v(91.05, -2400) * mm});
            skLineSegment(sketch, "E314", {"start": v(91.05, -2400) * mm, "end": v(-108.95, -2400) * mm});
            skLineSegment(sketch, "E315", {"start": v(-108.95, -2400) * mm, "end": v(-108.95, 96.97) * mm});
            skLineSegment(sketch, "E316", {"start": v(-3905, 2673.45) * mm, "end": v(1154.25, 2673.45) * mm});
            skLineSegment(sketch, "E317", {"start": v(-2408.95, 96.97) * mm, "end": v(-2408.95, 446.97) * mm});
            skLineSegment(sketch, "E318", {"start": v(-2408.95, 446.97) * mm, "end": v(2391.05, 446.97) * mm});
            skLineSegment(sketch, "E319", {"start": v(2391.05, 446.97) * mm, "end": v(2391.05, 96.97) * mm});
            skLineSegment(sketch, "E320", {"start": v(2391.05, 96.97) * mm, "end": v(-2408.95, 96.97) * mm});
            skCircle(sketch, "E321", {"center": v(-2099.35, 763.71) * mm, "radius": 225 * mm});
            skCircle(sketch, "E322", {"center": v(-1416.22, 763.71) * mm, "radius": 225 * mm});
            skCircle(sketch, "E323", {"center": v(-718.85, 763.71) * mm, "radius": 225 * mm});
            skCircle(sketch, "E324", {"center": v(6.98, 763.71) * mm, "radius": 225 * mm});
            skCircle(sketch, "E325", {"center": v(692.96, 763.71) * mm, "radius": 225 * mm});
            skCircle(sketch, "E326", {"center": v(1398.87, 763.71) * mm, "radius": 225 * mm});
            skCircle(sketch, "E327", {"center": v(2079.16, 763.71) * mm, "radius": 225 * mm});
            skLineSegment(sketch, "E328", {"start": v(641.05, -653.03) * mm, "end": v(641.05, -2112.15) * mm});
            skLineSegment(sketch, "E329", {"start": v(641.05, -2112.15) * mm, "end": v(191.05, -2112.15) * mm});
            skLineSegment(sketch, "E330", {"start": v(2191.06, -203.03) * mm, "end": v(2191.06, -653.03) * mm});
            skLineSegment(sketch, "E331", {"start": v(2191.06, -653.03) * mm, "end": v(641.05, -653.03) * mm});
            skCircle(sketch, "E332", {"center": v(2174.52, -1653.03) * mm, "radius": 225 * mm});
            skCircle(sketch, "E333", {"center": v(1641.05, -410.86) * mm, "radius": 125 * mm});
            skCircle(sketch, "E334", {"center": v(1041.05, -414.5) * mm, "radius": 125 * mm});
            skLineSegment(sketch, "E335", {"start": v(1823.05, -1830.03) * mm, "end": v(1823.05, -738.03) * mm});
            skArc(sketch, "E336", {"start": v(1823.05, -738.03) * mm, "mid": v(1821.58, -734.5) * mm, "end": v(1818.05, -733.03) * mm});
            skLineSegment(sketch, "E337", {"start": v(1818.05, -733.03) * mm, "end": v(726.05, -733.03) * mm});
            skArc(sketch, "E338", {"start": v(726.05, -733.03) * mm, "mid": v(722.51, -734.5) * mm, "end": v(721.05, -738.03) * mm});
            skLineSegment(sketch, "E339", {"start": v(721.05, -738.03) * mm, "end": v(721.05, -1830.03) * mm});
            skArc(sketch, "E340", {"start": v(721.05, -1830.03) * mm, "mid": v(722.51, -1833.56) * mm, "end": v(726.05, -1835.03) * mm});
            skLineSegment(sketch, "E341", {"start": v(726.05, -1835.03) * mm, "end": v(1818.05, -1835.03) * mm});
            skArc(sketch, "E342", {"start": v(1818.05, -1835.03) * mm, "mid": v(1821.58, -1833.56) * mm, "end": v(1823.05, -1830.03) * mm});
            skCircle(sketch, "E343", {"center": v(2174.52, -1053.03) * mm, "radius": 225 * mm});
            skCircle(sketch, "E344", {"center": v(1641.05, -2186.5) * mm, "radius": 225 * mm});
            skCircle(sketch, "E345", {"center": v(1041.05, -2186.5) * mm, "radius": 225 * mm});
            skCircle(sketch, "E346", {"center": v(398.87, -1653.03) * mm, "radius": 125 * mm});
            skCircle(sketch, "E347", {"center": v(402.52, -1053.03) * mm, "radius": 125 * mm});
            skLineSegment(sketch, "E348", {"start": v(-3905, 2673.45) * mm, "end": v(-3905, 2073.45) * mm});
            skLineSegment(sketch, "E349", {"start": v(1154.25, 2823.45) * mm, "end": v(1154.25, 2073.45) * mm});
            skLineSegment(sketch, "E350", {"start": v(1154.25, 2073.45) * mm, "end": v(2404.25, 2073.45) * mm});
            skLineSegment(sketch, "E351", {"start": v(2404.25, 2073.45) * mm, "end": v(2404.25, 2823.45) * mm});
            skLineSegment(sketch, "E352", {"start": v(2404.25, 2823.45) * mm, "end": v(2324.25, 2823.45) * mm});
            skLineSegment(sketch, "E353", {"start": v(2324.25, 2823.45) * mm, "end": v(2324.25, 2153.45) * mm});
            skLineSegment(sketch, "E354", {"start": v(1234.25, 2823.45) * mm, "end": v(1234.25, 2153.45) * mm});
            skLineSegment(sketch, "E355", {"start": v(1234.25, 2153.45) * mm, "end": v(2324.25, 2153.45) * mm});
            skLineSegment(sketch, "E356", {"start": v(1154.25, 2823.45) * mm, "end": v(1234.25, 2823.45) * mm});
            skCircle(sketch, "E357", {"center": v(-1289.95, -1284.03) * mm, "radius": 75 * mm});
            skCircle(sketch, "E358", {"center": v(-1289.95, -1284.03) * mm, "radius": 375 * mm});
            skCircle(sketch, "E359", {"center": v(1272.05, -1284.03) * mm, "radius": 75 * mm});
            skCircle(sketch, "E360", {"center": v(1272.05, -1284.03) * mm, "radius": 375 * mm});
            skCircle(sketch, "E361", {"center": v(-5313.66, 822.79) * mm, "radius": 75 * mm});
            skCircle(sketch, "E362", {"center": v(-5313.66, 0) * mm, "radius": 75 * mm});
            skCircle(sketch, "E363", {"center": v(-5313.66, -867.26) * mm, "radius": 75 * mm});
            skCircle(sketch, "E364", {"center": v(-2012.95, -5020.31) * mm, "radius": 75 * mm});
            skCircle(sketch, "E365", {"center": v(-4597.67, -2047.33) * mm, "radius": 75 * mm});
            skCircle(sketch, "E366", {"center": v(-3864.78, -3793.23) * mm, "radius": 75 * mm});
            skCircle(sketch, "E367", {"center": v(-3326.8, -3272.34) * mm, "radius": 75 * mm});
            skCircle(sketch, "E368", {"center": v(2776.75, -4864.68) * mm, "radius": 75 * mm});
            skCircle(sketch, "E369", {"center": v(2238.78, -4343.8) * mm, "radius": 75 * mm});
            skCircle(sketch, "E370", {"center": v(4249.76, -3405.9) * mm, "radius": 75 * mm});
            skCircle(sketch, "E371", {"center": v(3711.8, -2885.01) * mm, "radius": 75 * mm});
            skCircle(sketch, "E372", {"center": v(-5313.66, 822.79) * mm, "radius": 125 * mm});
            skCircle(sketch, "E373", {"center": v(-5313.66, 0) * mm, "radius": 125 * mm});
            skCircle(sketch, "E374", {"center": v(-5313.66, -867.26) * mm, "radius": 125 * mm});
            skCircle(sketch, "E375", {"center": v(-4597.67, -2047.33) * mm, "radius": 125 * mm});
            skCircle(sketch, "E376", {"center": v(-3864.78, -3793.23) * mm, "radius": 125 * mm});
            skCircle(sketch, "E377", {"center": v(-3326.8, -3272.34) * mm, "radius": 125 * mm});
            skCircle(sketch, "E378", {"center": v(-2012.95, -5020.31) * mm, "radius": 125 * mm});
            skCircle(sketch, "E379", {"center": v(2776.75, -4864.68) * mm, "radius": 125 * mm});
            skCircle(sketch, "E380", {"center": v(2238.78, -4343.8) * mm, "radius": 125 * mm});
            skCircle(sketch, "E381", {"center": v(4249.76, -3405.9) * mm, "radius": 125 * mm});
            skCircle(sketch, "E382", {"center": v(3711.8, -2885.01) * mm, "radius": 125 * mm});
            skSolve(sketch);
        }
        {
            var Q0;
            {var subQ37=sQuery(id+"F0.wireOp",EDGE,"E15");Q0=makeQuery(id+"F0.imprint","IMPRINT",FACE,{"disambiguationData":[TD([[makeQuery(id+"F0.imprint","IMPRINT",EDGE,{"derivedFrom":subQ37}),1.0]])]});}
            cPlane(context, id + "F1", {"entities" : qUnion([Q0]), "cplaneType" : CPlaneType.OFFSET, "offset" : 470 * mm, "width" : 150 * mm, "height" : 150 * mm});
        }
        {
            var Q0;
            {var subQ37=sQuery(id+"F0.wireOp",EDGE,"E15");Q0=makeQuery(id+"F0.imprint","IMPRINT",FACE,{"disambiguationData":[TD([[makeQuery(id+"F0.imprint","IMPRINT",EDGE,{"derivedFrom":subQ37}),1.0]])]});}
            cPlane(context, id + "F2", {"entities" : qUnion([Q0]), "cplaneType" : CPlaneType.OFFSET, "offset" : 740 * mm, "width" : 150 * mm, "height" : 150 * mm});
        }
        {
            var Q0;
            Q0=makeQuery(id+"F0.imprint","IMPRINT",FACE,{"disambiguationData":[TD([[makeQuery(id+"F0.imprint","IMPRINT",EDGE,{"derivedFrom":sQuery(id+"F0.wireOp",EDGE,"E13")}),1.0]])]});
            cPlane(context, id + "F3", {"entities" : qUnion([Q0]), "cplaneType" : CPlaneType.OFFSET, "offset" : 900 * mm, "width" : 150 * mm, "height" : 150 * mm});
        }
        {
            var Q0;
            Q0=makeQuery(id+"F0.imprint","IMPRINT",FACE,{"disambiguationData":[TD([[makeQuery(id+"F0.imprint","IMPRINT",EDGE,{"derivedFrom":sQuery(id+"F0.wireOp",EDGE,"E13")}),1.0]])]});
            cPlane(context, id + "F4", {"entities" : qUnion([Q0]), "cplaneType" : CPlaneType.OFFSET, "offset" : 1200 * mm, "width" : 150 * mm, "height" : 150 * mm});
        }
        {
            var Q0;
            Q0=makeQuery(id+"F0.imprint","IMPRINT",FACE,{"disambiguationData":[TD([[makeQuery(id+"F0.imprint","IMPRINT",EDGE,{"derivedFrom":sQuery(id+"F0.wireOp",EDGE,"E13")}),1.0]])]});
            cPlane(context, id + "F5", {"entities" : qUnion([Q0]), "cplaneType" : CPlaneType.OFFSET, "offset" : 1550 * mm, "width" : 150 * mm, "height" : 150 * mm});
        }
        {
            var Q0;
            Q0=qCreatedBy(id+"F4.planeOp",FACE);
            var sketch = newSketch(context, id + "F6", { "sketchPlane" : qUnion([Q0])});
            skLineSegment(sketch, "E383.0.0", {"start": v(-108.95, 96.97) * mm, "end": v(-2306.97, 96.97) * mm});
            skLineSegment(sketch, "E383.0.1", {"start": v(-2306.97, 96.97) * mm, "end": v(-2408.95, 96.97) * mm});
            skLineSegment(sketch, "E383.0.2", {"start": v(-2408.95, 96.97) * mm, "end": v(-2408.95, -103.03) * mm});
            skLineSegment(sketch, "E383.0.3", {"start": v(-2408.95, -103.03) * mm, "end": v(-2208.97, -103.03) * mm});
            skLineSegment(sketch, "E383.0.4", {"start": v(-2208.97, -103.03) * mm, "end": v(-108.95, -103.03) * mm});
            skLineSegment(sketch, "E383.0.5", {"start": v(-108.95, -103.03) * mm, "end": v(-108.95, 96.97) * mm});
            skLineSegment(sketch, "E384.0.0", {"start": v(91.05, -103.03) * mm, "end": v(91.05, 96.97) * mm});
            skLineSegment(sketch, "E384.0.1", {"start": v(91.05, 96.97) * mm, "end": v(-108.95, 96.97) * mm});
            skLineSegment(sketch, "E384.0.2", {"start": v(-108.95, 96.97) * mm, "end": v(-108.95, -103.03) * mm});
            skLineSegment(sketch, "E384.0.3", {"start": v(-108.95, -103.03) * mm, "end": v(91.05, -103.03) * mm});
            skLineSegment(sketch, "E385.0.0", {"start": v(2191.06, -103.03) * mm, "end": v(2391.05, -103.03) * mm});
            skLineSegment(sketch, "E385.0.1", {"start": v(2391.05, -103.03) * mm, "end": v(2391.05, 96.97) * mm});
            skLineSegment(sketch, "E385.0.2", {"start": v(2391.05, 96.97) * mm, "end": v(2289.06, 96.97) * mm});
            skLineSegment(sketch, "E385.0.3", {"start": v(2289.06, 96.97) * mm, "end": v(91.05, 96.97) * mm});
            skLineSegment(sketch, "E385.0.4", {"start": v(91.05, 96.97) * mm, "end": v(91.05, -103.03) * mm});
            skLineSegment(sketch, "E385.0.5", {"start": v(91.05, -103.03) * mm, "end": v(2191.06, -103.03) * mm});
            skLineSegment(sketch, "E386.0.0", {"start": v(91.05, -2112.15) * mm, "end": v(91.05, -103.03) * mm});
            skLineSegment(sketch, "E386.0.1", {"start": v(91.05, -103.03) * mm, "end": v(-108.95, -103.03) * mm});
            skLineSegment(sketch, "E386.0.2", {"start": v(-108.95, -103.03) * mm, "end": v(-108.95, -2112.15) * mm});
            skLineSegment(sketch, "E386.0.3", {"start": v(-108.95, -2112.15) * mm, "end": v(-108.95, -2400) * mm});
            skLineSegment(sketch, "E386.0.4", {"start": v(-108.95, -2400) * mm, "end": v(91.05, -2400) * mm});
            skLineSegment(sketch, "E386.0.5", {"start": v(91.05, -2400) * mm, "end": v(91.05, -2112.15) * mm});
            skSolve(sketch);
        }
        {
            var Q0;
            Q0 = qSketchRegion(id + "F6", true);
            extrude(context, id + "F7", {"entities" : qUnion([Q0]), "oppositeDirection" : true, "depth" : 1200 * mm, "offsetDistance" : 25 * mm});
        }
        {
            var Q0;
            Q0=qCreatedBy(id+"F3.planeOp",FACE);
            var sketch = newSketch(context, id + "F8", { "sketchPlane" : qUnion([Q0])});
            skLineSegment(sketch, "E387.0.0", {"start": v(-108.95, -103.03) * mm, "end": v(-2208.97, -103.03) * mm});
            skLineSegment(sketch, "E387.0.1", {"start": v(-2208.97, -103.03) * mm, "end": v(-2208.97, -203.03) * mm});
            skLineSegment(sketch, "E387.0.2", {"start": v(-2208.97, -203.03) * mm, "end": v(-208.95, -203.03) * mm});
            skLineSegment(sketch, "E387.0.3", {"start": v(-208.95, -203.03) * mm, "end": v(-208.95, -2112.15) * mm});
            skLineSegment(sketch, "E387.0.4", {"start": v(-208.95, -2112.15) * mm, "end": v(-108.95, -2112.15) * mm});
            skLineSegment(sketch, "E387.0.5", {"start": v(-108.95, -2112.15) * mm, "end": v(-108.95, -103.03) * mm});
            skLineSegment(sketch, "E388.0.0", {"start": v(91.05, -2112.15) * mm, "end": v(191.05, -2112.15) * mm});
            skLineSegment(sketch, "E388.0.1", {"start": v(191.05, -2112.15) * mm, "end": v(191.05, -203.03) * mm});
            skLineSegment(sketch, "E388.0.2", {"start": v(191.05, -203.03) * mm, "end": v(2191.06, -203.03) * mm});
            skLineSegment(sketch, "E388.0.3", {"start": v(2191.06, -203.03) * mm, "end": v(2191.06, -103.03) * mm});
            skLineSegment(sketch, "E388.0.4", {"start": v(2191.06, -103.03) * mm, "end": v(91.05, -103.03) * mm});
            skLineSegment(sketch, "E388.0.5", {"start": v(91.05, -103.03) * mm, "end": v(91.05, -2112.15) * mm});
            skSolve(sketch);
        }
        {
            var Q0;
            Q0 = qSketchRegion(id + "F8", true);
            extrude(context, id + "F9", {"entities" : qUnion([Q0]), "operationType" : NewBodyOperationType.ADD, "oppositeDirection" : true, "depth" : 900 * mm, "offsetDistance" : 25 * mm});
        }
        {
            var Q0;
            Q0=qCreatedBy(id+"F1.planeOp",FACE);
            var sketch = newSketch(context, id + "F10", { "sketchPlane" : qUnion([Q0])});
            skLineSegment(sketch, "E389.0.0", {"start": v(-658.95, -653.03) * mm, "end": v(-658.95, -2112.15) * mm});
            skLineSegment(sketch, "E389.0.1", {"start": v(-658.95, -2112.15) * mm, "end": v(-208.95, -2112.15) * mm});
            skLineSegment(sketch, "E389.0.2", {"start": v(-208.95, -2112.15) * mm, "end": v(-208.95, -203.03) * mm});
            skLineSegment(sketch, "E389.0.3", {"start": v(-208.95, -203.03) * mm, "end": v(-2208.97, -203.03) * mm});
            skLineSegment(sketch, "E389.0.4", {"start": v(-2208.97, -203.03) * mm, "end": v(-2208.97, -653.03) * mm});
            skLineSegment(sketch, "E389.0.5", {"start": v(-2208.97, -653.03) * mm, "end": v(-658.95, -653.03) * mm});
            skLineSegment(sketch, "E390.0.0", {"start": v(2191.06, -653.03) * mm, "end": v(2191.06, -203.03) * mm});
            skLineSegment(sketch, "E390.0.1", {"start": v(2191.06, -203.03) * mm, "end": v(191.05, -203.03) * mm});
            skLineSegment(sketch, "E390.0.2", {"start": v(191.05, -203.03) * mm, "end": v(191.05, -2112.15) * mm});
            skLineSegment(sketch, "E390.0.3", {"start": v(191.05, -2112.15) * mm, "end": v(641.05, -2112.15) * mm});
            skLineSegment(sketch, "E390.0.4", {"start": v(641.05, -2112.15) * mm, "end": v(641.05, -653.03) * mm});
            skLineSegment(sketch, "E390.0.5", {"start": v(641.05, -653.03) * mm, "end": v(2191.06, -653.03) * mm});
            skSolve(sketch);
        }
        {
            var Q0;
            Q0 = qSketchRegion(id + "F10", true);
            extrude(context, id + "F11", {"entities" : qUnion([Q0]), "operationType" : NewBodyOperationType.ADD, "oppositeDirection" : true, "depth" : 470 * mm, "offsetDistance" : 25 * mm});
        }
        {
            var Q0;
            Q0=qCreatedBy(id+"F2.planeOp",FACE);
            var sketch = newSketch(context, id + "F12", { "sketchPlane" : qUnion([Q0])});
            skLineSegment(sketch, "E391.0.0", {"start": v(-4968.66, 1172.79) * mm, "end": v(-5658.66, 1172.79) * mm});
            skArc(sketch, "E391.0.1", {"start": v(-5658.66, 1172.79) * mm, "mid": v(-5662.2, 1171.32) * mm, "end": v(-5663.66, 1167.79) * mm});
            skLineSegment(sketch, "E391.0.2", {"start": v(-5663.66, 1167.79) * mm, "end": v(-5663.66, 477.79) * mm});
            skArc(sketch, "E391.0.3", {"start": v(-5663.66, 477.79) * mm, "mid": v(-5662.2, 474.25) * mm, "end": v(-5658.66, 472.79) * mm});
            skLineSegment(sketch, "E391.0.4", {"start": v(-5658.66, 472.79) * mm, "end": v(-4968.66, 472.79) * mm});
            skArc(sketch, "E391.0.5", {"start": v(-4968.66, 472.79) * mm, "mid": v(-4965.12, 474.25) * mm, "end": v(-4963.66, 477.79) * mm});
            skLineSegment(sketch, "E391.0.6", {"start": v(-4963.66, 477.79) * mm, "end": v(-4963.66, 1167.79) * mm});
            skArc(sketch, "E391.0.7", {"start": v(-4963.66, 1167.79) * mm, "mid": v(-4965.12, 1171.32) * mm, "end": v(-4968.66, 1172.79) * mm});
            skLineSegment(sketch, "E392.0.0", {"start": v(-4968.66, 350) * mm, "end": v(-5658.66, 350) * mm});
            skArc(sketch, "E392.0.1", {"start": v(-5658.66, 350) * mm, "mid": v(-5662.2, 348.54) * mm, "end": v(-5663.66, 345) * mm});
            skLineSegment(sketch, "E392.0.2", {"start": v(-5663.66, 345) * mm, "end": v(-5663.66, -345) * mm});
            skArc(sketch, "E392.0.3", {"start": v(-5663.66, -345) * mm, "mid": v(-5662.2, -348.54) * mm, "end": v(-5658.66, -350) * mm});
            skLineSegment(sketch, "E392.0.4", {"start": v(-5658.66, -350) * mm, "end": v(-4968.66, -350) * mm});
            skArc(sketch, "E392.0.5", {"start": v(-4968.66, -350) * mm, "mid": v(-4965.12, -348.54) * mm, "end": v(-4963.66, -345) * mm});
            skLineSegment(sketch, "E392.0.6", {"start": v(-4963.66, -345) * mm, "end": v(-4963.66, 345) * mm});
            skArc(sketch, "E392.0.7", {"start": v(-4963.66, 345) * mm, "mid": v(-4965.12, 348.54) * mm, "end": v(-4968.66, 350) * mm});
            skLineSegment(sketch, "E393.0.0", {"start": v(-4968.66, -517.26) * mm, "end": v(-5658.66, -517.26) * mm});
            skArc(sketch, "E393.0.1", {"start": v(-5658.66, -517.26) * mm, "mid": v(-5662.2, -518.73) * mm, "end": v(-5663.66, -522.26) * mm});
            skLineSegment(sketch, "E393.0.2", {"start": v(-5663.66, -522.26) * mm, "end": v(-5663.66, -1212.26) * mm});
            skArc(sketch, "E393.0.3", {"start": v(-5663.66, -1212.26) * mm, "mid": v(-5662.2, -1215.8) * mm, "end": v(-5658.66, -1217.26) * mm});
            skLineSegment(sketch, "E393.0.4", {"start": v(-5658.66, -1217.26) * mm, "end": v(-4968.66, -1217.26) * mm});
            skArc(sketch, "E393.0.5", {"start": v(-4968.66, -1217.26) * mm, "mid": v(-4965.12, -1215.8) * mm, "end": v(-4963.66, -1212.26) * mm});
            skLineSegment(sketch, "E393.0.6", {"start": v(-4963.66, -1212.26) * mm, "end": v(-4963.66, -522.26) * mm});
            skArc(sketch, "E393.0.7", {"start": v(-4963.66, -522.26) * mm, "mid": v(-4965.12, -518.73) * mm, "end": v(-4968.66, -517.26) * mm});
            skLineSegment(sketch, "E394.0.0", {"start": v(-4601.2, -1555.9) * mm, "end": v(-5089.1, -2043.8) * mm});
            skArc(sketch, "E394.0.1", {"start": v(-5089.1, -2043.8) * mm, "mid": v(-5090.57, -2047.33) * mm, "end": v(-5089.1, -2050.87) * mm});
            skLineSegment(sketch, "E394.0.2", {"start": v(-5089.1, -2050.87) * mm, "end": v(-4601.2, -2538.77) * mm});
            skArc(sketch, "E394.0.3", {"start": v(-4601.2, -2538.77) * mm, "mid": v(-4597.67, -2540.24) * mm, "end": v(-4594.13, -2538.77) * mm});
            skLineSegment(sketch, "E394.0.4", {"start": v(-4594.13, -2538.77) * mm, "end": v(-4106.23, -2050.87) * mm});
            skArc(sketch, "E394.0.5", {"start": v(-4106.23, -2050.87) * mm, "mid": v(-4104.77, -2047.33) * mm, "end": v(-4106.23, -2043.8) * mm});
            skLineSegment(sketch, "E394.0.6", {"start": v(-4106.23, -2043.8) * mm, "end": v(-4594.13, -1555.9) * mm});
            skArc(sketch, "E394.0.7", {"start": v(-4594.13, -1555.9) * mm, "mid": v(-4597.67, -1554.43) * mm, "end": v(-4601.2, -1555.9) * mm});
            skLineSegment(sketch, "E395.0.0", {"start": v(-3818.25, -3275.87) * mm, "end": v(-3330.34, -3763.78) * mm});
            skArc(sketch, "E395.0.1", {"start": v(-3330.34, -3763.78) * mm, "mid": v(-3326.8, -3765.24) * mm, "end": v(-3323.27, -3763.78) * mm});
            skLineSegment(sketch, "E395.0.2", {"start": v(-3323.27, -3763.78) * mm, "end": v(-2835.37, -3275.87) * mm});
            skArc(sketch, "E395.0.3", {"start": v(-2835.37, -3275.87) * mm, "mid": v(-2833.9, -3272.34) * mm, "end": v(-2835.37, -3268.8) * mm});
            skLineSegment(sketch, "E395.0.4", {"start": v(-2835.37, -3268.8) * mm, "end": v(-3323.27, -2780.9) * mm});
            skArc(sketch, "E395.0.5", {"start": v(-3323.27, -2780.9) * mm, "mid": v(-3326.8, -2779.43) * mm, "end": v(-3330.34, -2780.9) * mm});
            skLineSegment(sketch, "E395.0.6", {"start": v(-3330.34, -2780.9) * mm, "end": v(-3818.25, -3268.8) * mm});
            skArc(sketch, "E395.0.7", {"start": v(-3818.25, -3268.8) * mm, "mid": v(-3819.71, -3272.34) * mm, "end": v(-3818.25, -3275.87) * mm});
            skLineSegment(sketch, "E396.0.0", {"start": v(-4356.22, -3796.76) * mm, "end": v(-3868.31, -4284.67) * mm});
            skArc(sketch, "E396.0.1", {"start": v(-3868.31, -4284.67) * mm, "mid": v(-3864.78, -4286.13) * mm, "end": v(-3861.24, -4284.67) * mm});
            skLineSegment(sketch, "E396.0.2", {"start": v(-3861.24, -4284.67) * mm, "end": v(-3373.34, -3796.76) * mm});
            skArc(sketch, "E396.0.3", {"start": v(-3373.34, -3796.76) * mm, "mid": v(-3371.87, -3793.23) * mm, "end": v(-3373.34, -3789.7) * mm});
            skLineSegment(sketch, "E396.0.4", {"start": v(-3373.34, -3789.7) * mm, "end": v(-3861.24, -3301.79) * mm});
            skArc(sketch, "E396.0.5", {"start": v(-3861.24, -3301.79) * mm, "mid": v(-3864.78, -3300.33) * mm, "end": v(-3868.31, -3301.79) * mm});
            skLineSegment(sketch, "E396.0.6", {"start": v(-3868.31, -3301.79) * mm, "end": v(-4356.22, -3789.7) * mm});
            skArc(sketch, "E396.0.7", {"start": v(-4356.22, -3789.7) * mm, "mid": v(-4357.68, -3793.23) * mm, "end": v(-4356.22, -3796.76) * mm});
            skArc(sketch, "E397.0.0", {"start": v(-2362.95, -5365.31) * mm, "mid": v(-2361.48, -5368.85) * mm, "end": v(-2357.95, -5370.31) * mm});
            skLineSegment(sketch, "E397.0.1", {"start": v(-2357.95, -5370.31) * mm, "end": v(-1667.95, -5370.31) * mm});
            skArc(sketch, "E397.0.2", {"start": v(-1667.95, -5370.31) * mm, "mid": v(-1664.41, -5368.85) * mm, "end": v(-1662.95, -5365.31) * mm});
            skLineSegment(sketch, "E397.0.3", {"start": v(-1662.95, -5365.31) * mm, "end": v(-1662.95, -4675.31) * mm});
            skArc(sketch, "E397.0.4", {"start": v(-1662.95, -4675.31) * mm, "mid": v(-1664.41, -4671.78) * mm, "end": v(-1667.95, -4670.31) * mm});
            skLineSegment(sketch, "E397.0.5", {"start": v(-1667.95, -4670.31) * mm, "end": v(-2357.95, -4670.31) * mm});
            skArc(sketch, "E397.0.6", {"start": v(-2357.95, -4670.31) * mm, "mid": v(-2361.48, -4671.78) * mm, "end": v(-2362.95, -4675.31) * mm});
            skLineSegment(sketch, "E397.0.7", {"start": v(-2362.95, -4675.31) * mm, "end": v(-2362.95, -5365.31) * mm});
            skArc(sketch, "E398.0.0", {"start": v(2773.22, -5356.12) * mm, "mid": v(2776.75, -5357.59) * mm, "end": v(2780.29, -5356.12) * mm});
            skLineSegment(sketch, "E398.0.1", {"start": v(2780.29, -5356.12) * mm, "end": v(3268.2, -4868.22) * mm});
            skArc(sketch, "E398.0.2", {"start": v(3268.2, -4868.22) * mm, "mid": v(3269.66, -4864.68) * mm, "end": v(3268.2, -4861.15) * mm});
            skLineSegment(sketch, "E398.0.3", {"start": v(3268.2, -4861.15) * mm, "end": v(2780.29, -4373.24) * mm});
            skArc(sketch, "E398.0.4", {"start": v(2780.29, -4373.24) * mm, "mid": v(2776.75, -4371.78) * mm, "end": v(2773.22, -4373.24) * mm});
            skLineSegment(sketch, "E398.0.5", {"start": v(2773.22, -4373.24) * mm, "end": v(2285.31, -4861.15) * mm});
            skArc(sketch, "E398.0.6", {"start": v(2285.31, -4861.15) * mm, "mid": v(2283.85, -4864.68) * mm, "end": v(2285.31, -4868.22) * mm});
            skLineSegment(sketch, "E398.0.7", {"start": v(2285.31, -4868.22) * mm, "end": v(2773.22, -5356.12) * mm});
            skArc(sketch, "E399.0.0", {"start": v(2235.25, -4835.23) * mm, "mid": v(2238.78, -4836.7) * mm, "end": v(2242.32, -4835.23) * mm});
            skLineSegment(sketch, "E399.0.1", {"start": v(2242.32, -4835.23) * mm, "end": v(2730.22, -4347.33) * mm});
            skArc(sketch, "E399.0.2", {"start": v(2730.22, -4347.33) * mm, "mid": v(2731.69, -4343.8) * mm, "end": v(2730.22, -4340.26) * mm});
            skLineSegment(sketch, "E399.0.3", {"start": v(2730.22, -4340.26) * mm, "end": v(2242.32, -3852.35) * mm});
            skArc(sketch, "E399.0.4", {"start": v(2242.32, -3852.35) * mm, "mid": v(2238.78, -3850.89) * mm, "end": v(2235.25, -3852.35) * mm});
            skLineSegment(sketch, "E399.0.5", {"start": v(2235.25, -3852.35) * mm, "end": v(1747.34, -4340.26) * mm});
            skArc(sketch, "E399.0.6", {"start": v(1747.34, -4340.26) * mm, "mid": v(1745.88, -4343.8) * mm, "end": v(1747.34, -4347.33) * mm});
            skLineSegment(sketch, "E399.0.7", {"start": v(1747.34, -4347.33) * mm, "end": v(2235.25, -4835.23) * mm});
            skArc(sketch, "E400.0.0", {"start": v(4246.23, -3897.34) * mm, "mid": v(4249.76, -3898.8) * mm, "end": v(4253.3, -3897.34) * mm});
            skLineSegment(sketch, "E400.0.1", {"start": v(4253.3, -3897.34) * mm, "end": v(4741.2, -3409.44) * mm});
            skArc(sketch, "E400.0.2", {"start": v(4741.2, -3409.44) * mm, "mid": v(4742.67, -3405.9) * mm, "end": v(4741.2, -3402.37) * mm});
            skLineSegment(sketch, "E400.0.3", {"start": v(4741.2, -3402.37) * mm, "end": v(4253.3, -2914.47) * mm});
            skArc(sketch, "E400.0.4", {"start": v(4253.3, -2914.47) * mm, "mid": v(4249.76, -2913) * mm, "end": v(4246.23, -2914.47) * mm});
            skLineSegment(sketch, "E400.0.5", {"start": v(4246.23, -2914.47) * mm, "end": v(3758.32, -3402.37) * mm});
            skArc(sketch, "E400.0.6", {"start": v(3758.32, -3402.37) * mm, "mid": v(3756.86, -3405.9) * mm, "end": v(3758.32, -3409.44) * mm});
            skLineSegment(sketch, "E400.0.7", {"start": v(3758.32, -3409.44) * mm, "end": v(4246.23, -3897.34) * mm});
            skLineSegment(sketch, "E401.0.0", {"start": v(726.05, -1835.03) * mm, "end": v(1818.05, -1835.03) * mm});
            skArc(sketch, "E401.0.1", {"start": v(1818.05, -1835.03) * mm, "mid": v(1821.58, -1833.56) * mm, "end": v(1823.05, -1830.03) * mm});
            skLineSegment(sketch, "E401.0.2", {"start": v(1823.05, -1830.03) * mm, "end": v(1823.05, -738.03) * mm});
            skArc(sketch, "E401.0.3", {"start": v(1823.05, -738.03) * mm, "mid": v(1821.58, -734.5) * mm, "end": v(1818.05, -733.03) * mm});
            skLineSegment(sketch, "E401.0.4", {"start": v(1818.05, -733.03) * mm, "end": v(726.05, -733.03) * mm});
            skArc(sketch, "E401.0.5", {"start": v(726.05, -733.03) * mm, "mid": v(722.51, -734.5) * mm, "end": v(721.05, -738.03) * mm});
            skLineSegment(sketch, "E401.0.6", {"start": v(721.05, -738.03) * mm, "end": v(721.05, -1830.03) * mm});
            skArc(sketch, "E401.0.7", {"start": v(721.05, -1830.03) * mm, "mid": v(722.51, -1833.56) * mm, "end": v(726.05, -1835.03) * mm});
            skArc(sketch, "E402.0.0", {"start": v(-1840.95, -1830.03) * mm, "mid": v(-1839.49, -1833.56) * mm, "end": v(-1835.95, -1835.03) * mm});
            skLineSegment(sketch, "E402.0.1", {"start": v(-1835.95, -1835.03) * mm, "end": v(-743.95, -1835.03) * mm});
            skArc(sketch, "E402.0.2", {"start": v(-743.95, -1835.03) * mm, "mid": v(-740.42, -1833.56) * mm, "end": v(-738.95, -1830.03) * mm});
            skLineSegment(sketch, "E402.0.3", {"start": v(-738.95, -1830.03) * mm, "end": v(-738.95, -738.03) * mm});
            skArc(sketch, "E402.0.4", {"start": v(-738.95, -738.03) * mm, "mid": v(-740.42, -734.5) * mm, "end": v(-743.95, -733.03) * mm});
            skLineSegment(sketch, "E402.0.5", {"start": v(-743.95, -733.03) * mm, "end": v(-1835.95, -733.03) * mm});
            skArc(sketch, "E402.0.6", {"start": v(-1835.95, -733.03) * mm, "mid": v(-1839.49, -734.5) * mm, "end": v(-1840.95, -738.03) * mm});
            skLineSegment(sketch, "E402.0.7", {"start": v(-1840.95, -738.03) * mm, "end": v(-1840.95, -1830.03) * mm});
            skArc(sketch, "E403.0.0", {"start": v(3708.26, -3376.45) * mm, "mid": v(3711.8, -3377.92) * mm, "end": v(3715.33, -3376.45) * mm});
            skLineSegment(sketch, "E403.0.1", {"start": v(3715.33, -3376.45) * mm, "end": v(4203.23, -2888.55) * mm});
            skArc(sketch, "E403.0.2", {"start": v(4203.23, -2888.55) * mm, "mid": v(4204.7, -2885.01) * mm, "end": v(4203.23, -2881.48) * mm});
            skLineSegment(sketch, "E403.0.3", {"start": v(4203.23, -2881.48) * mm, "end": v(3715.33, -2393.58) * mm});
            skArc(sketch, "E403.0.4", {"start": v(3715.33, -2393.58) * mm, "mid": v(3711.8, -2392.11) * mm, "end": v(3708.26, -2393.58) * mm});
            skLineSegment(sketch, "E403.0.5", {"start": v(3708.26, -2393.58) * mm, "end": v(3220.35, -2881.48) * mm});
            skArc(sketch, "E403.0.6", {"start": v(3220.35, -2881.48) * mm, "mid": v(3218.89, -2885.01) * mm, "end": v(3220.35, -2888.55) * mm});
            skLineSegment(sketch, "E403.0.7", {"start": v(3220.35, -2888.55) * mm, "end": v(3708.26, -3376.45) * mm});
            skSolve(sketch);
        }
        {
            var Q0;
            Q0 = qSketchRegion(id + "F12", true);
            extrude(context, id + "F13", {"entities" : qUnion([Q0]), "oppositeDirection" : true, "depth" : 60 * mm, "offsetDistance" : 25 * mm});
        }
        {
            var Q0;
            Q0=qCreatedBy(makeId("Top.planeOp"),FACE);
            var sketch = newSketch(context, id + "F14", { "sketchPlane" : qUnion([Q0])});
            skArc(sketch, "E404.0.0", {"start": v(-1104.68, 2546.22) * mm, "mid": v(-1103.06, 2544.6) * mm, "end": v(-1100.76, 2544.6) * mm});
            skLineSegment(sketch, "E404.0.1", {"start": v(-1100.76, 2544.6) * mm, "end": v(-1013.92, 2580.57) * mm});
            skArc(sketch, "E404.0.2", {"start": v(-1013.92, 2580.57) * mm, "mid": v(-1012.3, 2582.2) * mm, "end": v(-1012.3, 2584.5) * mm});
            skLineSegment(sketch, "E404.0.3", {"start": v(-1012.3, 2584.5) * mm, "end": v(-1048.26, 2671.34) * mm});
            skArc(sketch, "E404.0.4", {"start": v(-1048.26, 2671.34) * mm, "mid": v(-1049.89, 2672.96) * mm, "end": v(-1052.18, 2672.96) * mm});
            skLineSegment(sketch, "E404.0.5", {"start": v(-1052.18, 2672.96) * mm, "end": v(-1139.03, 2636.99) * mm});
            skArc(sketch, "E404.0.6", {"start": v(-1139.03, 2636.99) * mm, "mid": v(-1140.65, 2635.36) * mm, "end": v(-1140.65, 2633.07) * mm});
            skLineSegment(sketch, "E404.0.7", {"start": v(-1140.65, 2633.07) * mm, "end": v(-1104.68, 2546.22) * mm});
            skLineSegment(sketch, "E405.0.0", {"start": v(1013.92, 2580.57) * mm, "end": v(1100.76, 2544.6) * mm});
            skArc(sketch, "E405.0.1", {"start": v(1100.76, 2544.6) * mm, "mid": v(1103.06, 2544.6) * mm, "end": v(1104.68, 2546.22) * mm});
            skLineSegment(sketch, "E405.0.2", {"start": v(1104.68, 2546.22) * mm, "end": v(1140.65, 2633.07) * mm});
            skArc(sketch, "E405.0.3", {"start": v(1140.65, 2633.07) * mm, "mid": v(1140.65, 2635.36) * mm, "end": v(1139.03, 2636.99) * mm});
            skLineSegment(sketch, "E405.0.4", {"start": v(1139.03, 2636.99) * mm, "end": v(1052.18, 2672.96) * mm});
            skArc(sketch, "E405.0.5", {"start": v(1052.18, 2672.96) * mm, "mid": v(1049.89, 2672.96) * mm, "end": v(1048.26, 2671.34) * mm});
            skLineSegment(sketch, "E405.0.6", {"start": v(1048.26, 2671.34) * mm, "end": v(1012.3, 2584.5) * mm});
            skArc(sketch, "E405.0.7", {"start": v(1012.3, 2584.5) * mm, "mid": v(1012.3, 2582.2) * mm, "end": v(1013.92, 2580.57) * mm});
            skLineSegment(sketch, "E406.0.0", {"start": v(-2580.57, 1013.92) * mm, "end": v(-2544.6, 1100.76) * mm});
            skArc(sketch, "E406.0.1", {"start": v(-2544.6, 1100.76) * mm, "mid": v(-2544.6, 1103.06) * mm, "end": v(-2546.22, 1104.68) * mm});
            skLineSegment(sketch, "E406.0.2", {"start": v(-2546.22, 1104.68) * mm, "end": v(-2633.07, 1140.65) * mm});
            skArc(sketch, "E406.0.3", {"start": v(-2633.07, 1140.65) * mm, "mid": v(-2635.36, 1140.65) * mm, "end": v(-2636.99, 1139.03) * mm});
            skLineSegment(sketch, "E406.0.4", {"start": v(-2636.99, 1139.03) * mm, "end": v(-2672.96, 1052.18) * mm});
            skArc(sketch, "E406.0.5", {"start": v(-2672.96, 1052.18) * mm, "mid": v(-2672.96, 1049.89) * mm, "end": v(-2671.34, 1048.26) * mm});
            skLineSegment(sketch, "E406.0.6", {"start": v(-2671.34, 1048.26) * mm, "end": v(-2584.5, 1012.3) * mm});
            skArc(sketch, "E406.0.7", {"start": v(-2584.5, 1012.3) * mm, "mid": v(-2582.2, 1012.3) * mm, "end": v(-2580.57, 1013.92) * mm});
            skArc(sketch, "E407.0.0", {"start": v(-2546.22, -1104.68) * mm, "mid": v(-2544.6, -1103.06) * mm, "end": v(-2544.6, -1100.76) * mm});
            skLineSegment(sketch, "E407.0.1", {"start": v(-2544.6, -1100.76) * mm, "end": v(-2580.57, -1013.92) * mm});
            skArc(sketch, "E407.0.2", {"start": v(-2580.57, -1013.92) * mm, "mid": v(-2582.2, -1012.3) * mm, "end": v(-2584.5, -1012.3) * mm});
            skLineSegment(sketch, "E407.0.3", {"start": v(-2584.5, -1012.3) * mm, "end": v(-2671.34, -1048.26) * mm});
            skArc(sketch, "E407.0.4", {"start": v(-2671.34, -1048.26) * mm, "mid": v(-2672.96, -1049.89) * mm, "end": v(-2672.96, -1052.18) * mm});
            skLineSegment(sketch, "E407.0.5", {"start": v(-2672.96, -1052.18) * mm, "end": v(-2636.99, -1139.03) * mm});
            skArc(sketch, "E407.0.6", {"start": v(-2636.99, -1139.03) * mm, "mid": v(-2635.36, -1140.65) * mm, "end": v(-2633.07, -1140.65) * mm});
            skLineSegment(sketch, "E407.0.7", {"start": v(-2633.07, -1140.65) * mm, "end": v(-2546.22, -1104.68) * mm});
            skLineSegment(sketch, "E408.0.0", {"start": v(-1013.92, -2580.57) * mm, "end": v(-1100.76, -2544.6) * mm});
            skArc(sketch, "E408.0.1", {"start": v(-1100.76, -2544.6) * mm, "mid": v(-1103.06, -2544.6) * mm, "end": v(-1104.68, -2546.22) * mm});
            skLineSegment(sketch, "E408.0.2", {"start": v(-1104.68, -2546.22) * mm, "end": v(-1140.65, -2633.07) * mm});
            skArc(sketch, "E408.0.3", {"start": v(-1140.65, -2633.07) * mm, "mid": v(-1140.65, -2635.36) * mm, "end": v(-1139.03, -2636.99) * mm});
            skLineSegment(sketch, "E408.0.4", {"start": v(-1139.03, -2636.99) * mm, "end": v(-1052.18, -2672.96) * mm});
            skArc(sketch, "E408.0.5", {"start": v(-1052.18, -2672.96) * mm, "mid": v(-1049.89, -2672.96) * mm, "end": v(-1048.26, -2671.34) * mm});
            skLineSegment(sketch, "E408.0.6", {"start": v(-1048.26, -2671.34) * mm, "end": v(-1012.3, -2584.5) * mm});
            skArc(sketch, "E408.0.7", {"start": v(-1012.3, -2584.5) * mm, "mid": v(-1012.3, -2582.2) * mm, "end": v(-1013.92, -2580.57) * mm});
            skArc(sketch, "E409.0.0", {"start": v(1104.68, -2546.22) * mm, "mid": v(1103.06, -2544.6) * mm, "end": v(1100.76, -2544.6) * mm});
            skLineSegment(sketch, "E409.0.1", {"start": v(1100.76, -2544.6) * mm, "end": v(1013.92, -2580.57) * mm});
            skArc(sketch, "E409.0.2", {"start": v(1013.92, -2580.57) * mm, "mid": v(1012.3, -2582.2) * mm, "end": v(1012.3, -2584.5) * mm});
            skLineSegment(sketch, "E409.0.3", {"start": v(1012.3, -2584.5) * mm, "end": v(1048.26, -2671.34) * mm});
            skArc(sketch, "E409.0.4", {"start": v(1048.26, -2671.34) * mm, "mid": v(1049.89, -2672.96) * mm, "end": v(1052.18, -2672.96) * mm});
            skLineSegment(sketch, "E409.0.5", {"start": v(1052.18, -2672.96) * mm, "end": v(1139.03, -2636.99) * mm});
            skArc(sketch, "E409.0.6", {"start": v(1139.03, -2636.99) * mm, "mid": v(1140.65, -2635.36) * mm, "end": v(1140.65, -2633.07) * mm});
            skLineSegment(sketch, "E409.0.7", {"start": v(1140.65, -2633.07) * mm, "end": v(1104.68, -2546.22) * mm});
            skLineSegment(sketch, "E410.0.0", {"start": v(2580.57, -1013.92) * mm, "end": v(2544.6, -1100.76) * mm});
            skArc(sketch, "E410.0.1", {"start": v(2544.6, -1100.76) * mm, "mid": v(2544.6, -1103.06) * mm, "end": v(2546.22, -1104.68) * mm});
            skLineSegment(sketch, "E410.0.2", {"start": v(2546.22, -1104.68) * mm, "end": v(2633.07, -1140.65) * mm});
            skArc(sketch, "E410.0.3", {"start": v(2633.07, -1140.65) * mm, "mid": v(2635.36, -1140.65) * mm, "end": v(2636.99, -1139.03) * mm});
            skLineSegment(sketch, "E410.0.4", {"start": v(2636.99, -1139.03) * mm, "end": v(2672.96, -1052.18) * mm});
            skArc(sketch, "E410.0.5", {"start": v(2672.96, -1052.18) * mm, "mid": v(2672.96, -1049.89) * mm, "end": v(2671.34, -1048.26) * mm});
            skLineSegment(sketch, "E410.0.6", {"start": v(2671.34, -1048.26) * mm, "end": v(2584.5, -1012.3) * mm});
            skArc(sketch, "E410.0.7", {"start": v(2584.5, -1012.3) * mm, "mid": v(2582.2, -1012.3) * mm, "end": v(2580.57, -1013.92) * mm});
            skArc(sketch, "E411.0.0", {"start": v(2546.22, 1104.68) * mm, "mid": v(2544.6, 1103.06) * mm, "end": v(2544.6, 1100.76) * mm});
            skLineSegment(sketch, "E411.0.1", {"start": v(2544.6, 1100.76) * mm, "end": v(2580.57, 1013.92) * mm});
            skArc(sketch, "E411.0.2", {"start": v(2580.57, 1013.92) * mm, "mid": v(2582.2, 1012.3) * mm, "end": v(2584.5, 1012.3) * mm});
            skLineSegment(sketch, "E411.0.3", {"start": v(2584.5, 1012.3) * mm, "end": v(2671.34, 1048.26) * mm});
            skArc(sketch, "E411.0.4", {"start": v(2671.34, 1048.26) * mm, "mid": v(2672.96, 1049.89) * mm, "end": v(2672.96, 1052.18) * mm});
            skLineSegment(sketch, "E411.0.5", {"start": v(2672.96, 1052.18) * mm, "end": v(2636.99, 1139.03) * mm});
            skArc(sketch, "E411.0.6", {"start": v(2636.99, 1139.03) * mm, "mid": v(2635.36, 1140.65) * mm, "end": v(2633.07, 1140.65) * mm});
            skLineSegment(sketch, "E411.0.7", {"start": v(2633.07, 1140.65) * mm, "end": v(2546.22, 1104.68) * mm});
            skSolve(sketch);
        }
        {
            var Q0;
            Q0 = qSketchRegion(id + "F14", true);
            extrude(context, id + "F15", {"entities" : qUnion([Q0]), "depth" : 2400 * mm, "offsetDistance" : 25 * mm});
        }
        {
            var Q0;
            Q0=qCreatedBy(makeId("Top.planeOp"),FACE);
            var sketch = newSketch(context, id + "F16", { "sketchPlane" : qUnion([Q0])});
            skLineSegment(sketch, "E412.0.0", {"start": v(-4225.73, 4195.92) * mm, "end": v(-4147.94, 4118.13) * mm});
            skLineSegment(sketch, "E412.0.1", {"start": v(-4147.94, 4118.13) * mm, "end": v(-3521.08, 4745) * mm});
            skLineSegment(sketch, "E412.0.2", {"start": v(-3521.08, 4745) * mm, "end": v(-860, 4745) * mm});
            skLineSegment(sketch, "E412.0.3", {"start": v(-860, 4745) * mm, "end": v(-860, 4595) * mm});
            skLineSegment(sketch, "E412.0.4", {"start": v(-860, 4595) * mm, "end": v(860, 4595) * mm});
            skLineSegment(sketch, "E412.0.5", {"start": v(860, 4595) * mm, "end": v(860, 4745) * mm});
            skLineSegment(sketch, "E412.0.6", {"start": v(860, 4745) * mm, "end": v(1682.6, 4745) * mm});
            skLineSegment(sketch, "E412.0.7", {"start": v(1682.6, 4745) * mm, "end": v(2248.29, 4179.31) * mm});
            skLineSegment(sketch, "E412.0.8", {"start": v(2248.29, 4179.31) * mm, "end": v(2389.7, 4320.74) * mm});
            skLineSegment(sketch, "E412.0.9", {"start": v(2389.7, 4320.74) * mm, "end": v(2326.07, 4384.38) * mm});
            skLineSegment(sketch, "E412.0.10", {"start": v(2326.07, 4384.38) * mm, "end": v(2248.29, 4306.6) * mm});
            skLineSegment(sketch, "E412.0.11", {"start": v(2248.29, 4306.6) * mm, "end": v(1719.88, 4835) * mm});
            skLineSegment(sketch, "E412.0.12", {"start": v(1719.88, 4835) * mm, "end": v(770, 4835) * mm});
            skLineSegment(sketch, "E412.0.13", {"start": v(770, 4835) * mm, "end": v(770, 4685) * mm});
            skLineSegment(sketch, "E412.0.14", {"start": v(770, 4685) * mm, "end": v(-770, 4685) * mm});
            skLineSegment(sketch, "E412.0.15", {"start": v(-770, 4685) * mm, "end": v(-770, 4835) * mm});
            skLineSegment(sketch, "E412.0.16", {"start": v(-770, 4835) * mm, "end": v(-3431.08, 4835) * mm});
            skLineSegment(sketch, "E412.0.17", {"start": v(-3431.08, 4835) * mm, "end": v(-2421.08, 5845) * mm});
            skLineSegment(sketch, "E412.0.18", {"start": v(-2421.08, 5845) * mm, "end": v(-2466.64, 5955) * mm});
            skLineSegment(sketch, "E412.0.19", {"start": v(-2466.64, 5955) * mm, "end": v(-4225.73, 4195.92) * mm});
            skLineSegment(sketch, "E413.0.0", {"start": v(-5845, 2421.08) * mm, "end": v(-5420.74, 2845.34) * mm});
            skLineSegment(sketch, "E413.0.1", {"start": v(-5420.74, 2845.34) * mm, "end": v(-5498.52, 2923.12) * mm});
            skLineSegment(sketch, "E413.0.2", {"start": v(-5498.52, 2923.12) * mm, "end": v(-5922.78, 2498.86) * mm});
            skLineSegment(sketch, "E413.0.3", {"start": v(-5922.78, 2498.86) * mm, "end": v(-5845, 2421.08) * mm});
            skLineSegment(sketch, "E414.0.0", {"start": v(-5845, 1400) * mm, "end": v(-5845, 2421.08) * mm});
            skLineSegment(sketch, "E414.0.1", {"start": v(-5845, 2421.08) * mm, "end": v(-5922.78, 2498.86) * mm});
            skLineSegment(sketch, "E414.0.2", {"start": v(-5922.78, 2498.86) * mm, "end": v(-5955, 2466.64) * mm});
            skLineSegment(sketch, "E414.0.3", {"start": v(-5955, 2466.64) * mm, "end": v(-5955, 1510) * mm});
            skLineSegment(sketch, "E414.0.4", {"start": v(-5955, 1510) * mm, "end": v(-6555, 1510) * mm});
            skLineSegment(sketch, "E414.0.5", {"start": v(-6555, 1510) * mm, "end": v(-6555, 1400) * mm});
            skLineSegment(sketch, "E414.0.6", {"start": v(-6555, 1400) * mm, "end": v(-6445, 1400) * mm});
            skLineSegment(sketch, "E414.0.7", {"start": v(-6445, 1400) * mm, "end": v(-5955, 1400) * mm});
            skLineSegment(sketch, "E414.0.8", {"start": v(-5955, 1400) * mm, "end": v(-5845, 1400) * mm});
            skLineSegment(sketch, "E415.0.0", {"start": v(-6555, -100) * mm, "end": v(-6445, -100) * mm});
            skLineSegment(sketch, "E415.0.1", {"start": v(-6445, -100) * mm, "end": v(-6445, 100) * mm});
            skLineSegment(sketch, "E415.0.2", {"start": v(-6445, 100) * mm, "end": v(-6555, 100) * mm});
            skLineSegment(sketch, "E415.0.3", {"start": v(-6555, 100) * mm, "end": v(-6555, -100) * mm});
            skLineSegment(sketch, "E416.0.0", {"start": v(-5955, -1510) * mm, "end": v(-5955, -2466.64) * mm});
            skLineSegment(sketch, "E416.0.1", {"start": v(-5955, -2466.64) * mm, "end": v(-5660.39, -2761.25) * mm});
            skLineSegment(sketch, "E416.0.2", {"start": v(-5660.39, -2761.25) * mm, "end": v(-5582.6, -2683.47) * mm});
            skLineSegment(sketch, "E416.0.3", {"start": v(-5582.6, -2683.47) * mm, "end": v(-5845, -2421.08) * mm});
            skLineSegment(sketch, "E416.0.4", {"start": v(-5845, -2421.08) * mm, "end": v(-5845, -1400) * mm});
            skLineSegment(sketch, "E416.0.5", {"start": v(-5845, -1400) * mm, "end": v(-5955, -1400) * mm});
            skLineSegment(sketch, "E416.0.6", {"start": v(-5955, -1400) * mm, "end": v(-6445, -1400) * mm});
            skLineSegment(sketch, "E416.0.7", {"start": v(-6445, -1400) * mm, "end": v(-6555, -1400) * mm});
            skLineSegment(sketch, "E416.0.8", {"start": v(-6555, -1400) * mm, "end": v(-6555, -1510) * mm});
            skLineSegment(sketch, "E416.0.9", {"start": v(-6555, -1510) * mm, "end": v(-5955, -1510) * mm});
            skLineSegment(sketch, "E417.0.0", {"start": v(-4309.82, -3956.26) * mm, "end": v(-4387.6, -4034.04) * mm});
            skLineSegment(sketch, "E417.0.1", {"start": v(-4387.6, -4034.04) * mm, "end": v(-4034.04, -4387.6) * mm});
            skLineSegment(sketch, "E417.0.2", {"start": v(-4034.04, -4387.6) * mm, "end": v(-3956.26, -4309.82) * mm});
            skLineSegment(sketch, "E417.0.3", {"start": v(-3956.26, -4309.82) * mm, "end": v(-4309.82, -3956.26) * mm});
            skLineSegment(sketch, "E418.0.0", {"start": v(-1600, -5955) * mm, "end": v(-1600, -5845) * mm});
            skLineSegment(sketch, "E418.0.1", {"start": v(-1600, -5845) * mm, "end": v(-2421.08, -5845) * mm});
            skLineSegment(sketch, "E418.0.2", {"start": v(-2421.08, -5845) * mm, "end": v(-2683.47, -5582.6) * mm});
            skLineSegment(sketch, "E418.0.3", {"start": v(-2683.47, -5582.6) * mm, "end": v(-2761.25, -5660.39) * mm});
            skLineSegment(sketch, "E418.0.4", {"start": v(-2761.25, -5660.39) * mm, "end": v(-2466.64, -5955) * mm});
            skLineSegment(sketch, "E418.0.5", {"start": v(-2466.64, -5955) * mm, "end": v(-1600, -5955) * mm});
            skLineSegment(sketch, "E419.0.0", {"start": v(2421.08, -5845) * mm, "end": v(1600, -5845) * mm});
            skLineSegment(sketch, "E419.0.1", {"start": v(1600, -5845) * mm, "end": v(1600, -5955) * mm});
            skLineSegment(sketch, "E419.0.2", {"start": v(1600, -5955) * mm, "end": v(2466.64, -5955) * mm});
            skLineSegment(sketch, "E419.0.3", {"start": v(2466.64, -5955) * mm, "end": v(2761.25, -5660.39) * mm});
            skLineSegment(sketch, "E419.0.4", {"start": v(2761.25, -5660.39) * mm, "end": v(2683.47, -5582.6) * mm});
            skLineSegment(sketch, "E419.0.5", {"start": v(2683.47, -5582.6) * mm, "end": v(2421.08, -5845) * mm});
            skLineSegment(sketch, "E420.0.0", {"start": v(3956.26, -4309.82) * mm, "end": v(4034.04, -4387.6) * mm});
            skLineSegment(sketch, "E420.0.1", {"start": v(4034.04, -4387.6) * mm, "end": v(4387.6, -4034.04) * mm});
            skLineSegment(sketch, "E420.0.2", {"start": v(4387.6, -4034.04) * mm, "end": v(4309.82, -3956.26) * mm});
            skLineSegment(sketch, "E420.0.3", {"start": v(4309.82, -3956.26) * mm, "end": v(3956.26, -4309.82) * mm});
            skLineSegment(sketch, "E421.0.0", {"start": v(5582.6, -2683.47) * mm, "end": v(5660.39, -2761.25) * mm});
            skLineSegment(sketch, "E421.0.1", {"start": v(5660.39, -2761.25) * mm, "end": v(5955, -2466.64) * mm});
            skLineSegment(sketch, "E421.0.2", {"start": v(5955, -2466.64) * mm, "end": v(5955, 2466.64) * mm});
            skLineSegment(sketch, "E421.0.3", {"start": v(5955, 2466.64) * mm, "end": v(5845, 2421.08) * mm});
            skLineSegment(sketch, "E421.0.4", {"start": v(5845, 2421.08) * mm, "end": v(5845, -2421.08) * mm});
            skLineSegment(sketch, "E421.0.5", {"start": v(5845, -2421.08) * mm, "end": v(5582.6, -2683.47) * mm});
            skLineSegment(sketch, "E422.0.0", {"start": v(5955, 2466.64) * mm, "end": v(2466.64, 5955) * mm});
            skLineSegment(sketch, "E422.0.1", {"start": v(2466.64, 5955) * mm, "end": v(-2466.64, 5955) * mm});
            skLineSegment(sketch, "E422.0.2", {"start": v(-2466.64, 5955) * mm, "end": v(-2421.08, 5845) * mm});
            skLineSegment(sketch, "E422.0.3", {"start": v(-2421.08, 5845) * mm, "end": v(2421.08, 5845) * mm});
            skLineSegment(sketch, "E422.0.4", {"start": v(2421.08, 5845) * mm, "end": v(4757.13, 3508.95) * mm});
            skLineSegment(sketch, "E422.0.5", {"start": v(4757.13, 3508.95) * mm, "end": v(5845, 2421.08) * mm});
            skLineSegment(sketch, "E422.0.6", {"start": v(5845, 2421.08) * mm, "end": v(5955, 2466.64) * mm});
            skSolve(sketch);
        }
        {
            var Q0;
            Q0 = qSketchRegion(id + "F16", true);
            extrude(context, id + "F17", {"entities" : qUnion([Q0]), "depth" : 2400 * mm, "offsetDistance" : 25 * mm});
        }
        {
            var Q0;
            Q0=qCreatedBy(makeId("Top.planeOp"),FACE);
            cPlane(context, id + "F18", {"entities" : qUnion([Q0]), "cplaneType" : CPlaneType.OFFSET, "offset" : 1170 * mm, "width" : 150 * mm, "height" : 150 * mm});
        }
        {
            var Q0;
            Q0=qCreatedBy(id+"F18.planeOp",FACE);
            var sketch = newSketch(context, id + "F19", { "sketchPlane" : qUnion([Q0])});
            skLineSegment(sketch, "E423.0.0", {"start": v(1154.25, 2673.45) * mm, "end": v(-3905, 2673.45) * mm});
            skLineSegment(sketch, "E423.0.1", {"start": v(-3905, 2673.45) * mm, "end": v(-3905, 2073.45) * mm});
            skLineSegment(sketch, "E423.0.2", {"start": v(-3905, 2073.45) * mm, "end": v(1154.25, 2073.45) * mm});
            skLineSegment(sketch, "E423.0.3", {"start": v(1154.25, 2073.45) * mm, "end": v(1154.25, 2673.45) * mm});
            skSolve(sketch);
        }
        {
            var Q0;
            Q0 = qSketchRegion(id + "F19", true);
            extrude(context, id + "F20", {"entities" : qUnion([Q0]), "oppositeDirection" : true, "depth" : 80 * mm, "offsetDistance" : 25 * mm});
        }
        {
            var Q0;
            Q0=qCreatedBy(id+"F5.planeOp",FACE);
            var sketch = newSketch(context, id + "F21", { "sketchPlane" : qUnion([Q0])});
            skLineSegment(sketch, "E424.0.0", {"start": v(1154.25, 2673.45) * mm, "end": v(1154.25, 2073.45) * mm});
            skLineSegment(sketch, "E424.0.1", {"start": v(1154.25, 2073.45) * mm, "end": v(2404.25, 2073.45) * mm});
            skLineSegment(sketch, "E424.0.2", {"start": v(2404.25, 2073.45) * mm, "end": v(2404.25, 2823.45) * mm});
            skLineSegment(sketch, "E424.0.3", {"start": v(2404.25, 2823.45) * mm, "end": v(2324.25, 2823.45) * mm});
            skLineSegment(sketch, "E424.0.4", {"start": v(2324.25, 2823.45) * mm, "end": v(2324.25, 2153.45) * mm});
            skLineSegment(sketch, "E424.0.5", {"start": v(2324.25, 2153.45) * mm, "end": v(1234.25, 2153.45) * mm});
            skLineSegment(sketch, "E424.0.6", {"start": v(1234.25, 2153.45) * mm, "end": v(1234.25, 2823.45) * mm});
            skLineSegment(sketch, "E424.0.7", {"start": v(1234.25, 2823.45) * mm, "end": v(1154.25, 2823.45) * mm});
            skLineSegment(sketch, "E424.0.8", {"start": v(1154.25, 2823.45) * mm, "end": v(1154.25, 2673.45) * mm});
            skSolve(sketch);
        }
        {
            var Q0;
            Q0 = qSketchRegion(id + "F21", true);
            extrude(context, id + "F22", {"entities" : qUnion([Q0]), "operationType" : NewBodyOperationType.ADD, "oppositeDirection" : true, "depth" : 1550 * mm, "offsetDistance" : 25 * mm});
        }
        {
            var Q0;
            Q0=makeQuery(id+"F7.opExtrude","CAP_FACE",FACE,{"disambiguationData":[OSD([sQuery(id+"F6.wireOp",EDGE,"E383.0.0"),sQuery(id+"F6.wireOp",EDGE,"E383.0.1"),sQuery(id+"F6.wireOp",EDGE,"E383.0.2"),sQuery(id+"F6.wireOp",EDGE,"E383.0.3"),sQuery(id+"F6.wireOp",EDGE,"E383.0.4"),sQuery(id+"F6.wireOp",EDGE,"E384.0.1"),sQuery(id+"F6.wireOp",EDGE,"E385.0.0"),sQuery(id+"F6.wireOp",EDGE,"E385.0.1"),sQuery(id+"F6.wireOp",EDGE,"E385.0.2"),sQuery(id+"F6.wireOp",EDGE,"E385.0.3"),sQuery(id+"F6.wireOp",EDGE,"E385.0.5"),sQuery(id+"F6.wireOp",EDGE,"E386.0.0"),sQuery(id+"F6.wireOp",EDGE,"E386.0.2"),sQuery(id+"F6.wireOp",EDGE,"E386.0.3"),sQuery(id+"F6.wireOp",EDGE,"E386.0.4"),sQuery(id+"F6.wireOp",EDGE,"E386.0.5")])],"isStart":true});
            var Q1;
            Q1=makeQuery(id+"F7.opExtrude","SWEPT_FACE",FACE,{"disambiguationData":[OSD([sQuery(id+"F6.wireOp",EDGE,"E386.0.4")])]});
            var Q2;
            Q2=makeQuery(id+"F7.opExtrude","SWEPT_FACE",FACE,{"disambiguationData":[OSD([sQuery(id+"F6.wireOp",EDGE,"E385.0.1")])]});
            var Q3;
            Q3=makeQuery(id+"F7.opExtrude","SWEPT_FACE",FACE,{"disambiguationData":[OSD([sQuery(id+"F6.wireOp",EDGE,"E383.0.2")])]});
            fillet(context, id + "F23", {"entities" : qUnion([Q0, Q1, Q2, Q3]), "radius" : 3 * mm, "tangentPropagation" : true, "allowEdgeOverflow" : false});
        }
        {
            var Q0;
            Q0=qCreatedBy(id+"F18.planeOp",FACE);
            var sketch = newSketch(context, id + "F24", { "sketchPlane" : qUnion([Q0])});
            skLineSegment(sketch, "E425.0.0", {"start": v(-108.95, 96.97) * mm, "end": v(91.05, 96.97) * mm});
            skLineSegment(sketch, "E425.0.1", {"start": v(91.05, 96.97) * mm, "end": v(2289.06, 96.97) * mm});
            skLineSegment(sketch, "E425.0.2", {"start": v(2289.06, 96.97) * mm, "end": v(2391.05, 96.97) * mm});
            skLineSegment(sketch, "E425.0.3", {"start": v(2391.05, 96.97) * mm, "end": v(2391.05, 446.97) * mm});
            skLineSegment(sketch, "E425.0.4", {"start": v(2391.05, 446.97) * mm, "end": v(-2408.95, 446.97) * mm});
            skLineSegment(sketch, "E425.0.5", {"start": v(-2408.95, 446.97) * mm, "end": v(-2408.95, 96.97) * mm});
            skLineSegment(sketch, "E425.0.6", {"start": v(-2408.95, 96.97) * mm, "end": v(-2306.97, 96.97) * mm});
            skLineSegment(sketch, "E425.0.7", {"start": v(-2306.97, 96.97) * mm, "end": v(-108.95, 96.97) * mm});
            skSolve(sketch);
        }
        {
            var Q0;
            Q0 = qSketchRegion(id + "F24", true);
            extrude(context, id + "F25", {"entities" : qUnion([Q0]), "operationType" : NewBodyOperationType.ADD, "oppositeDirection" : true, "depth" : 80 * mm, "offsetDistance" : 25 * mm});
        }
        {
            var Q0;
            {var subQ37=sQuery(id+"F0.wireOp",EDGE,"E15");Q0=makeQuery(id+"F0.imprint","IMPRINT",FACE,{"disambiguationData":[TD([[makeQuery(id+"F0.imprint","IMPRINT",EDGE,{"derivedFrom":subQ37}),1.0]])]});}
            cPlane(context, id + "F26", {"entities" : qUnion([Q0]), "cplaneType" : CPlaneType.OFFSET, "offset" : 2400 * mm, "width" : 150 * mm, "height" : 150 * mm});
        }
        {
            var Q0;
            Q0=qCreatedBy(id+"F26.planeOp",FACE);
            var sketch = newSketch(context, id + "F27", { "sketchPlane" : qUnion([Q0])});
            skLineSegment(sketch, "E426.0.0", {"start": v(-5420.74, 2845.34) * mm, "end": v(-4147.94, 4118.13) * mm});
            skLineSegment(sketch, "E426.0.1", {"start": v(-4147.94, 4118.13) * mm, "end": v(-4225.73, 4195.92) * mm});
            skLineSegment(sketch, "E426.0.2", {"start": v(-4225.73, 4195.92) * mm, "end": v(-5498.52, 2923.12) * mm});
            skLineSegment(sketch, "E426.0.3", {"start": v(-5498.52, 2923.12) * mm, "end": v(-5420.74, 2845.34) * mm});
            skLineSegment(sketch, "E427.0.0", {"start": v(-6555, 100) * mm, "end": v(-6445, 100) * mm});
            skLineSegment(sketch, "E427.0.1", {"start": v(-6445, 100) * mm, "end": v(-6445, 1400) * mm});
            skLineSegment(sketch, "E427.0.2", {"start": v(-6445, 1400) * mm, "end": v(-6555, 1400) * mm});
            skLineSegment(sketch, "E427.0.3", {"start": v(-6555, 1400) * mm, "end": v(-6555, 100) * mm});
            skLineSegment(sketch, "E428.0", {"start": v(-6445, 1400) * mm, "end": v(-6445, 100) * mm});
            skLineSegment(sketch, "E429.0.0", {"start": v(-5582.6, -2683.47) * mm, "end": v(-5660.39, -2761.25) * mm});
            skLineSegment(sketch, "E429.0.1", {"start": v(-5660.39, -2761.25) * mm, "end": v(-4387.6, -4034.04) * mm});
            skLineSegment(sketch, "E429.0.2", {"start": v(-4387.6, -4034.04) * mm, "end": v(-4309.82, -3956.26) * mm});
            skLineSegment(sketch, "E429.0.3", {"start": v(-4309.82, -3956.26) * mm, "end": v(-5582.6, -2683.47) * mm});
            skLineSegment(sketch, "E430.0.0", {"start": v(-2761.25, -5660.39) * mm, "end": v(-2683.47, -5582.6) * mm});
            skLineSegment(sketch, "E430.0.1", {"start": v(-2683.47, -5582.6) * mm, "end": v(-3956.26, -4309.82) * mm});
            skLineSegment(sketch, "E430.0.2", {"start": v(-3956.26, -4309.82) * mm, "end": v(-4034.04, -4387.6) * mm});
            skLineSegment(sketch, "E430.0.3", {"start": v(-4034.04, -4387.6) * mm, "end": v(-2761.25, -5660.39) * mm});
            skLineSegment(sketch, "E431.0.0", {"start": v(3956.26, -4309.82) * mm, "end": v(2683.47, -5582.6) * mm});
            skLineSegment(sketch, "E431.0.1", {"start": v(2683.47, -5582.6) * mm, "end": v(2761.25, -5660.39) * mm});
            skLineSegment(sketch, "E431.0.2", {"start": v(2761.25, -5660.39) * mm, "end": v(4034.04, -4387.6) * mm});
            skLineSegment(sketch, "E431.0.3", {"start": v(4034.04, -4387.6) * mm, "end": v(3956.26, -4309.82) * mm});
            skLineSegment(sketch, "E432.0.0", {"start": v(5322.82, -2943.26) * mm, "end": v(4309.82, -3956.26) * mm});
            skLineSegment(sketch, "E432.0.1", {"start": v(4309.82, -3956.26) * mm, "end": v(4387.6, -4034.04) * mm});
            skLineSegment(sketch, "E432.0.2", {"start": v(4387.6, -4034.04) * mm, "end": v(5660.39, -2761.25) * mm});
            skLineSegment(sketch, "E432.0.3", {"start": v(5660.39, -2761.25) * mm, "end": v(5582.6, -2683.47) * mm});
            skLineSegment(sketch, "E432.0.4", {"start": v(5582.6, -2683.47) * mm, "end": v(5322.82, -2943.26) * mm});
            skLineSegment(sketch, "E433.0.0", {"start": v(-6445, -1400) * mm, "end": v(-6445, -100) * mm});
            skLineSegment(sketch, "E433.0.1", {"start": v(-6445, -100) * mm, "end": v(-6555, -100) * mm});
            skLineSegment(sketch, "E433.0.2", {"start": v(-6555, -100) * mm, "end": v(-6555, -1400) * mm});
            skLineSegment(sketch, "E433.0.3", {"start": v(-6555, -1400) * mm, "end": v(-6445, -1400) * mm});
            skLineSegment(sketch, "E434.trimOffspring", {"start": v(-6445, -100) * mm, "end": v(-6445, -1400) * mm});
            skSolve(sketch);
        }
        {
            var Q0;
            Q0 = qSketchRegion(id + "F27", true);
            extrude(context, id + "F28", {"entities" : qUnion([Q0]), "operationType" : NewBodyOperationType.ADD, "oppositeDirection" : true, "depth" : 600 * mm, "offsetDistance" : 25 * mm});
        }
        {
            var Q0;
            Q0=qCreatedBy(makeId("Top.planeOp"),FACE);
            var sketch = newSketch(context, id + "F29", { "sketchPlane" : qUnion([Q0])});
            skLineSegment(sketch, "E435.0.0", {"start": v(5322.82, -2943.26) * mm, "end": v(4309.82, -3956.26) * mm});
            skLineSegment(sketch, "E435.0.1", {"start": v(4309.82, -3956.26) * mm, "end": v(4387.6, -4034.04) * mm});
            skLineSegment(sketch, "E435.0.2", {"start": v(4387.6, -4034.04) * mm, "end": v(5660.39, -2761.25) * mm});
            skLineSegment(sketch, "E435.0.3", {"start": v(5660.39, -2761.25) * mm, "end": v(5582.6, -2683.47) * mm});
            skLineSegment(sketch, "E435.0.4", {"start": v(5582.6, -2683.47) * mm, "end": v(5322.82, -2943.26) * mm});
            skLineSegment(sketch, "E436.0.0", {"start": v(3956.26, -4309.82) * mm, "end": v(2683.47, -5582.6) * mm});
            skLineSegment(sketch, "E436.0.1", {"start": v(2683.47, -5582.6) * mm, "end": v(2761.25, -5660.39) * mm});
            skLineSegment(sketch, "E436.0.2", {"start": v(2761.25, -5660.39) * mm, "end": v(4034.04, -4387.6) * mm});
            skLineSegment(sketch, "E436.0.3", {"start": v(4034.04, -4387.6) * mm, "end": v(3956.26, -4309.82) * mm});
            skLineSegment(sketch, "E437.0.0", {"start": v(-5582.6, -2683.47) * mm, "end": v(-5660.39, -2761.25) * mm});
            skLineSegment(sketch, "E437.0.1", {"start": v(-5660.39, -2761.25) * mm, "end": v(-4387.6, -4034.04) * mm});
            skLineSegment(sketch, "E437.0.2", {"start": v(-4387.6, -4034.04) * mm, "end": v(-4309.82, -3956.26) * mm});
            skLineSegment(sketch, "E437.0.3", {"start": v(-4309.82, -3956.26) * mm, "end": v(-5582.6, -2683.47) * mm});
            skLineSegment(sketch, "E438.0.0", {"start": v(-2761.25, -5660.39) * mm, "end": v(-2683.47, -5582.6) * mm});
            skLineSegment(sketch, "E438.0.1", {"start": v(-2683.47, -5582.6) * mm, "end": v(-3956.26, -4309.82) * mm});
            skLineSegment(sketch, "E438.0.2", {"start": v(-3956.26, -4309.82) * mm, "end": v(-4034.04, -4387.6) * mm});
            skLineSegment(sketch, "E438.0.3", {"start": v(-4034.04, -4387.6) * mm, "end": v(-2761.25, -5660.39) * mm});
            skLineSegment(sketch, "E439.0.0", {"start": v(-6445, -1400) * mm, "end": v(-6445, -100) * mm});
            skLineSegment(sketch, "E439.0.1", {"start": v(-6445, -100) * mm, "end": v(-6555, -100) * mm});
            skLineSegment(sketch, "E439.0.2", {"start": v(-6555, -100) * mm, "end": v(-6555, -1400) * mm});
            skLineSegment(sketch, "E439.0.3", {"start": v(-6555, -1400) * mm, "end": v(-6445, -1400) * mm});
            skLineSegment(sketch, "E440.0.0", {"start": v(-6555, 100) * mm, "end": v(-6445, 100) * mm});
            skLineSegment(sketch, "E440.0.1", {"start": v(-6445, 100) * mm, "end": v(-6445, 1400) * mm});
            skLineSegment(sketch, "E440.0.2", {"start": v(-6445, 1400) * mm, "end": v(-6555, 1400) * mm});
            skLineSegment(sketch, "E440.0.3", {"start": v(-6555, 1400) * mm, "end": v(-6555, 100) * mm});
            skLineSegment(sketch, "E441.0.0", {"start": v(-5420.74, 2845.34) * mm, "end": v(-4147.94, 4118.13) * mm});
            skLineSegment(sketch, "E441.0.1", {"start": v(-4147.94, 4118.13) * mm, "end": v(-4225.73, 4195.92) * mm});
            skLineSegment(sketch, "E441.0.2", {"start": v(-4225.73, 4195.92) * mm, "end": v(-5498.52, 2923.12) * mm});
            skLineSegment(sketch, "E441.0.3", {"start": v(-5498.52, 2923.12) * mm, "end": v(-5420.74, 2845.34) * mm});
            skSolve(sketch);
        }
        {
            var Q0;
            Q0 = qSketchRegion(id + "F29", true);
            extrude(context, id + "F30", {"entities" : qUnion([Q0]), "operationType" : NewBodyOperationType.ADD, "depth" : 1100 * mm, "offsetDistance" : 25 * mm});
        }
        {
            var Q0;
            Q0=qCreatedBy(makeId("Top.planeOp"),FACE);
            var sketch = newSketch(context, id + "F31", { "sketchPlane" : qUnion([Q0])});
            skLineSegment(sketch, "E442.0.0", {"start": v(1154.25, 2673.45) * mm, "end": v(-3905, 2673.45) * mm, "construction": true});
            skLineSegment(sketch, "E442.0.1", {"start": v(-3905, 2673.45) * mm, "end": v(-3905, 2073.45) * mm, "construction": true});
            skLineSegment(sketch, "E442.0.2", {"start": v(-3905, 2073.45) * mm, "end": v(1154.25, 2073.45) * mm, "construction": true});
            skLineSegment(sketch, "E442.0.3", {"start": v(1154.25, 2073.45) * mm, "end": v(1154.25, 2673.45) * mm});
            skLineSegment(sketch, "E443.0", {"start": v(1134.25, 2653.45) * mm, "end": v(-3885, 2653.45) * mm});
            skLineSegment(sketch, "E443.1", {"start": v(1134.25, 2093.45) * mm, "end": v(1134.25, 2653.45) * mm});
            skLineSegment(sketch, "E443.2", {"start": v(-3885, 2093.45) * mm, "end": v(1134.25, 2093.45) * mm});
            skLineSegment(sketch, "E443.3", {"start": v(-3885, 2653.45) * mm, "end": v(-3885, 2093.45) * mm});
            skSolve(sketch);
        }
        {
            var Q0;
            Q0=makeQuery(id+"F31.imprint","IMPRINT",FACE,{"disambiguationData":[TD([[makeQuery(id+"F31.imprint","IMPRINT",EDGE,{"derivedFrom":sQuery(id+"F31.wireOp",EDGE,"E443.0")}),1.0]])]});
            var Q1;
            Q1=sQuery(id+"F31.wireOp",EDGE,"E442.0.2");
            var Q2;
            Q2=sQuery(id+"F31.wireOp",EDGE,"E442.0.1");
            var Q3;
            Q3=sQuery(id+"F31.wireOp",EDGE,"E442.0.0");
            var Q4;
            Q4=sQuery(id+"F31.wireOp",EDGE,"E442.0.3");
            extrude(context, id + "F32", {"entities" : qUnion([Q0]), "surfaceEntities" : qUnion([Q1, Q2, Q3, Q4]), "depth" : 1120 * mm, "offsetDistance" : 25 * mm});
        }
        {
            var Q0;
            Q0=qCreatedBy(id+"F1.planeOp",FACE);
            var sketch = newSketch(context, id + "F33", { "sketchPlane" : qUnion([Q0])});
            skLineSegment(sketch, "E444.0.0", {"start": v(-5955, 120.38) * mm, "end": v(-5955, 702.4) * mm});
            skArc(sketch, "E444.0.1", {"start": v(-5955, 702.4) * mm, "mid": v(-6113.66, 822.79) * mm, "end": v(-5955, 943.17) * mm});
            skLineSegment(sketch, "E444.0.2", {"start": v(-5955, 943.17) * mm, "end": v(-5955, 1400) * mm});
            skLineSegment(sketch, "E444.0.3", {"start": v(-5955, 1400) * mm, "end": v(-6445, 1400) * mm});
            skLineSegment(sketch, "E444.0.4", {"start": v(-6445, 1400) * mm, "end": v(-6445, 100) * mm});
            skLineSegment(sketch, "E444.0.5", {"start": v(-6445, 100) * mm, "end": v(-6445, -100) * mm});
            skLineSegment(sketch, "E444.0.6", {"start": v(-6445, -100) * mm, "end": v(-6445, -1400) * mm});
            skLineSegment(sketch, "E444.0.7", {"start": v(-6445, -1400) * mm, "end": v(-5955, -1400) * mm});
            skLineSegment(sketch, "E444.0.8", {"start": v(-5955, -1400) * mm, "end": v(-5955, -987.64) * mm});
            skArc(sketch, "E444.0.9", {"start": v(-5955, -987.64) * mm, "mid": v(-6113.66, -867.26) * mm, "end": v(-5955, -746.88) * mm});
            skLineSegment(sketch, "E444.0.10", {"start": v(-5955, -746.88) * mm, "end": v(-5955, -120.38) * mm});
            skArc(sketch, "E444.0.11", {"start": v(-5955, -120.38) * mm, "mid": v(-6113.66, 0) * mm, "end": v(-5955, 120.38) * mm});
            skArc(sketch, "E445.0.0", {"start": v(-5955, 943.17) * mm, "mid": v(-6113.66, 822.79) * mm, "end": v(-5955, 702.4) * mm});
            skLineSegment(sketch, "E445.0.1", {"start": v(-5955, 702.4) * mm, "end": v(-5955, 943.17) * mm});
            skArc(sketch, "E446.0.0", {"start": v(-5955, 120.38) * mm, "mid": v(-6113.66, 0) * mm, "end": v(-5955, -120.38) * mm});
            skLineSegment(sketch, "E446.0.1", {"start": v(-5955, -120.38) * mm, "end": v(-5955, 120.38) * mm});
            skArc(sketch, "E447.0.0", {"start": v(-5955, -746.88) * mm, "mid": v(-6113.66, -867.26) * mm, "end": v(-5955, -987.64) * mm});
            skLineSegment(sketch, "E447.0.1", {"start": v(-5955, -987.64) * mm, "end": v(-5955, -746.88) * mm});
            skCircle(sketch, "E448.0.0", {"center": v(-5074.97, -2524.63) * mm, "radius": 225 * mm});
            skCircle(sketch, "E449.0.0", {"center": v(-4120.37, -1570.04) * mm, "radius": 225 * mm});
            skCircle(sketch, "E450.0.0", {"center": v(-4638.66, -867.26) * mm, "radius": 225 * mm});
            skCircle(sketch, "E451.0.0", {"center": v(-4638.66, 0) * mm, "radius": 225 * mm});
            skCircle(sketch, "E452.0.0", {"center": v(-4638.66, 822.79) * mm, "radius": 225 * mm});
            skCircle(sketch, "E453.0.0", {"center": v(-4342.08, -3315.93) * mm, "radius": 225 * mm});
            skCircle(sketch, "E454.0.0", {"center": v(-3804.1, -2795.04) * mm, "radius": 225 * mm});
            skCircle(sketch, "E455.0.0", {"center": v(-2849.51, -3749.64) * mm, "radius": 225 * mm});
            skCircle(sketch, "E456.0.0", {"center": v(-3387.48, -4270.53) * mm, "radius": 225 * mm});
            skCircle(sketch, "E457.0.0", {"center": v(-2687.95, -5020.31) * mm, "radius": 225 * mm});
            skCircle(sketch, "E458.0.0", {"center": v(-1337.95, -5020.31) * mm, "radius": 225 * mm});
            skCircle(sketch, "E459.0.0", {"center": v(-1058.95, -2186.5) * mm, "radius": 225 * mm});
            skCircle(sketch, "E460.0.0", {"center": v(-1658.95, -2186.5) * mm, "radius": 225 * mm});
            skCircle(sketch, "E461.0.0", {"center": v(-2192.43, -1653.03) * mm, "radius": 225 * mm});
            skCircle(sketch, "E462.0.0", {"center": v(-2192.43, -1053.03) * mm, "radius": 225 * mm});
            skCircle(sketch, "E463.0", {"center": v(2174.52, -1053.03) * mm, "radius": 225 * mm});
            skCircle(sketch, "E464.0.0", {"center": v(2174.52, -1653.03) * mm, "radius": 225 * mm});
            skPoint(sketch, "E465.0", {"position": v(1641.05, -2186.5) * mm});
            skCircle(sketch, "E466.0.0", {"center": v(1041.05, -2186.5) * mm, "radius": 225 * mm});
            skCircle(sketch, "E467.0.0", {"center": v(1641.05, -2186.5) * mm, "radius": 225 * mm});
            skCircle(sketch, "E468.0.0", {"center": v(2299.45, -5341.98) * mm, "radius": 225 * mm});
            skCircle(sketch, "E469.0.0", {"center": v(1761.49, -4821.09) * mm, "radius": 225 * mm});
            skCircle(sketch, "E470.0.0", {"center": v(3254.05, -4387.39) * mm, "radius": 225 * mm});
            skCircle(sketch, "E471.0.0", {"center": v(2716.08, -3866.5) * mm, "radius": 225 * mm});
            skCircle(sketch, "E472.0.0", {"center": v(3234.5, -3362.31) * mm, "radius": 225 * mm});
            skCircle(sketch, "E473.0.0", {"center": v(3772.46, -3883.2) * mm, "radius": 225 * mm});
            skCircle(sketch, "E474.0.0", {"center": v(4727.06, -2928.6) * mm, "radius": 225 * mm});
            skCircle(sketch, "E475.0.0", {"center": v(4189.09, -2407.72) * mm, "radius": 225 * mm});
            skSolve(sketch);
        }
        {
            var Q0;
            Q0 = qSketchRegion(id + "F33", true);
            extrude(context, id + "F34", {"entities" : qUnion([Q0]), "operationType" : NewBodyOperationType.ADD, "oppositeDirection" : true, "depth" : 50 * mm, "offsetDistance" : 25 * mm});
        }
        {
            var Q0;
            {var subQ0=sQuery(id+"F0.wireOp",EDGE,"E88");var subQ3=sQuery(id+"F0.wireOp",EDGE,"E82");var subQ5=makeQuery(id+"F0.imprint","INTERSECT",VERTEX,{"derivedFrom":[subQ3,subQ0]});Q0=makeQuery(id+"F0.imprint","IMPRINT",FACE,{"disambiguationData":[TD([[makeQuery(id+"F0.imprint","IMPRINT",EDGE,{"disambiguationData":[TD([[subQ5,1.0]])],"derivedFrom":subQ3}),-1.0]])]});}
            cPlane(context, id + "F35", {"entities" : qUnion([Q0]), "cplaneType" : CPlaneType.OFFSET, "offset" : 800 * mm, "width" : 150 * mm, "height" : 150 * mm});
        }
        {
            var Q0;
            Q0=qCreatedBy(id+"F35.planeOp",FACE);
            var sketch = newSketch(context, id + "F36", { "sketchPlane" : qUnion([Q0])});
            skCircle(sketch, "E476.0.0", {"center": v(-2099.35, 763.71) * mm, "radius": 225 * mm});
            skCircle(sketch, "E477.0.0", {"center": v(-1416.22, 763.71) * mm, "radius": 225 * mm});
            skCircle(sketch, "E478.0.0", {"center": v(-718.85, 763.71) * mm, "radius": 225 * mm});
            skCircle(sketch, "E479.0.0", {"center": v(6.98, 763.71) * mm, "radius": 225 * mm});
            skCircle(sketch, "E480.0.0", {"center": v(692.96, 763.71) * mm, "radius": 225 * mm});
            skCircle(sketch, "E481.0.0", {"center": v(1398.87, 763.71) * mm, "radius": 225 * mm});
            skCircle(sketch, "E482.0.0", {"center": v(2079.16, 763.71) * mm, "radius": 225 * mm});
            skSolve(sketch);
        }
        {
            var Q0;
            Q0 = qSketchRegion(id + "F36", true);
            extrude(context, id + "F37", {"entities" : qUnion([Q0]), "oppositeDirection" : true, "depth" : 50 * mm, "offsetDistance" : 25 * mm});
        }
        {
            var Q0;
            Q0=qCreatedBy(makeId("Top.planeOp"),FACE);
            var sketch = newSketch(context, id + "F38", { "sketchPlane" : qUnion([Q0])});
            skCircle(sketch, "E483.0", {"center": v(-4638.66, 822.79) * mm, "radius": 50 * mm});
            skCircle(sketch, "E484.0", {"center": v(-4638.66, 0) * mm, "radius": 50 * mm});
            skCircle(sketch, "E485.0", {"center": v(-4638.66, -867.26) * mm, "radius": 50 * mm});
            skCircle(sketch, "E486.0", {"center": v(-4120.37, -1570.04) * mm, "radius": 50 * mm});
            skCircle(sketch, "E487.0", {"center": v(-5074.97, -2524.63) * mm, "radius": 50 * mm});
            skCircle(sketch, "E488.0", {"center": v(-4342.08, -3315.93) * mm, "radius": 50 * mm});
            skCircle(sketch, "E489.0", {"center": v(-3804.1, -2795.04) * mm, "radius": 50 * mm});
            skCircle(sketch, "E490.0", {"center": v(-3387.48, -4270.53) * mm, "radius": 50 * mm});
            skCircle(sketch, "E491.0", {"center": v(-2849.51, -3749.64) * mm, "radius": 50 * mm});
            skCircle(sketch, "E492.0", {"center": v(-2687.95, -5020.31) * mm, "radius": 50 * mm});
            skCircle(sketch, "E493.0", {"center": v(-1337.95, -5020.31) * mm, "radius": 50 * mm});
            skCircle(sketch, "E494.0", {"center": v(-2192.43, -1053.03) * mm, "radius": 50 * mm});
            skCircle(sketch, "E495.0", {"center": v(-2192.43, -1653.03) * mm, "radius": 50 * mm});
            skCircle(sketch, "E496.0", {"center": v(-1658.95, -2186.5) * mm, "radius": 50 * mm});
            skCircle(sketch, "E497.0", {"center": v(-1058.95, -2186.5) * mm, "radius": 50 * mm});
            skCircle(sketch, "E498.0", {"center": v(1041.05, -2186.5) * mm, "radius": 50 * mm});
            skCircle(sketch, "E499.0", {"center": v(1641.05, -2186.5) * mm, "radius": 50 * mm});
            skCircle(sketch, "E500.0", {"center": v(2174.52, -1653.03) * mm, "radius": 50 * mm});
            skCircle(sketch, "E501.0", {"center": v(2174.52, -1053.03) * mm, "radius": 50 * mm});
            skCircle(sketch, "E502.0", {"center": v(1761.49, -4821.09) * mm, "radius": 50 * mm});
            skCircle(sketch, "E503.0", {"center": v(2299.45, -5341.98) * mm, "radius": 50 * mm});
            skCircle(sketch, "E504.0", {"center": v(2716.08, -3866.5) * mm, "radius": 50 * mm});
            skCircle(sketch, "E505.0", {"center": v(3254.05, -4387.39) * mm, "radius": 50 * mm});
            skCircle(sketch, "E506.0", {"center": v(3234.5, -3362.31) * mm, "radius": 50 * mm});
            skCircle(sketch, "E507.0", {"center": v(4189.09, -2407.72) * mm, "radius": 50 * mm});
            skCircle(sketch, "E508.0", {"center": v(4727.06, -2928.6) * mm, "radius": 50 * mm});
            skCircle(sketch, "E509.0", {"center": v(3772.46, -3883.2) * mm, "radius": 50 * mm});
            skSolve(sketch);
        }
        {
            var Q0;
            Q0 = qSketchRegion(id + "F38", true);
            extrude(context, id + "F39", {"entities" : qUnion([Q0]), "depth" : 450 * mm, "offsetDistance" : 25 * mm});
        }
        {
            var Q0;
            Q0=qCreatedBy(makeId("Top.planeOp"),FACE);
            var sketch = newSketch(context, id + "F40", { "sketchPlane" : qUnion([Q0])});
            skCircle(sketch, "E510.0", {"center": v(-2099.35, 763.71) * mm, "radius": 50 * mm});
            skCircle(sketch, "E511.0", {"center": v(-1416.22, 763.71) * mm, "radius": 50 * mm});
            skCircle(sketch, "E512.0", {"center": v(-718.85, 763.71) * mm, "radius": 50 * mm});
            skCircle(sketch, "E513.0", {"center": v(6.98, 763.71) * mm, "radius": 50 * mm});
            skCircle(sketch, "E514.0", {"center": v(692.96, 763.71) * mm, "radius": 50 * mm});
            skCircle(sketch, "E515.0", {"center": v(1398.87, 763.71) * mm, "radius": 50 * mm});
            skCircle(sketch, "E516.0", {"center": v(2079.16, 763.71) * mm, "radius": 50 * mm});
            skSolve(sketch);
        }
        {
            var Q0;
            Q0 = qSketchRegion(id + "F40", true);
            extrude(context, id + "F41", {"entities" : qUnion([Q0]), "depth" : 780 * mm, "offsetDistance" : 25 * mm});
        }
        {
            var Q0;
            Q0=qCreatedBy(makeId("Top.planeOp"),FACE);
            var sketch = newSketch(context, id + "F42", { "sketchPlane" : qUnion([Q0])});
            skCircle(sketch, "E517.0", {"center": v(-3387.48, -4270.53) * mm, "radius": 225 * mm, "construction": true});
            skCircle(sketch, "E518.0.0", {"center": v(-2849.51, -3749.64) * mm, "radius": 225 * mm, "construction": true});
            skCircle(sketch, "E519.0.0", {"center": v(-4342.08, -3315.93) * mm, "radius": 225 * mm, "construction": true});
            skCircle(sketch, "E520.0.0", {"center": v(-3804.1, -2795.04) * mm, "radius": 225 * mm, "construction": true});
            skCircle(sketch, "E521.0.0", {"center": v(-5074.97, -2524.63) * mm, "radius": 225 * mm, "construction": true});
            skCircle(sketch, "E522.0.0", {"center": v(-4120.37, -1570.04) * mm, "radius": 225 * mm, "construction": true});
            skCircle(sketch, "E523.0.0", {"center": v(-4638.66, -867.26) * mm, "radius": 225 * mm, "construction": true});
            skCircle(sketch, "E524.0.0", {"center": v(-4638.66, 0) * mm, "radius": 225 * mm, "construction": true});
            skCircle(sketch, "E525.0.0", {"center": v(-4638.66, 822.79) * mm, "radius": 225 * mm, "construction": true});
            skCircle(sketch, "E526.0.0", {"center": v(-2687.95, -5020.31) * mm, "radius": 225 * mm, "construction": true});
            skCircle(sketch, "E527.0.0", {"center": v(-1337.95, -5020.31) * mm, "radius": 225 * mm, "construction": true});
            skCircle(sketch, "E528.0.0", {"center": v(-2012.95, -5020.31) * mm, "radius": 125 * mm});
            skCircle(sketch, "E529.0.0", {"center": v(-3864.78, -3793.23) * mm, "radius": 125 * mm});
            skCircle(sketch, "E530.0.0", {"center": v(-3326.8, -3272.34) * mm, "radius": 125 * mm});
            skCircle(sketch, "E531.0.0", {"center": v(-4597.67, -2047.33) * mm, "radius": 125 * mm});
            skCircle(sketch, "E532.0.0", {"center": v(-5313.66, -867.26) * mm, "radius": 125 * mm});
            skCircle(sketch, "E533.0", {"center": v(-5313.66, 0) * mm, "radius": 75 * mm});
            skCircle(sketch, "E534.0.0", {"center": v(-5313.66, 0) * mm, "radius": 125 * mm});
            skCircle(sketch, "E535.0", {"center": v(-5313.66, 822.79) * mm, "radius": 125 * mm});
            skCircle(sketch, "E536.0.0", {"center": v(-2192.43, -1053.03) * mm, "radius": 225 * mm, "construction": true});
            skCircle(sketch, "E537.0.0", {"center": v(-2192.43, -1653.03) * mm, "radius": 225 * mm, "construction": true});
            skCircle(sketch, "E538.0.0", {"center": v(-1658.95, -2186.5) * mm, "radius": 225 * mm, "construction": true});
            skCircle(sketch, "E539.0.0", {"center": v(-1058.95, -2186.5) * mm, "radius": 225 * mm, "construction": true});
            skCircle(sketch, "E540.0.0", {"center": v(1041.05, -2186.5) * mm, "radius": 225 * mm, "construction": true});
            skCircle(sketch, "E541.0.0", {"center": v(1641.05, -2186.5) * mm, "radius": 225 * mm, "construction": true});
            skCircle(sketch, "E542.0.0", {"center": v(2174.52, -1653.03) * mm, "radius": 225 * mm, "construction": true});
            skCircle(sketch, "E543.0.0", {"center": v(2174.52, -1053.03) * mm, "radius": 225 * mm, "construction": true});
            skCircle(sketch, "E544.0.0", {"center": v(2299.45, -5341.98) * mm, "radius": 225 * mm, "construction": true});
            skCircle(sketch, "E545.0.0", {"center": v(1761.49, -4821.09) * mm, "radius": 225 * mm, "construction": true});
            skCircle(sketch, "E546.0.0", {"center": v(2238.78, -4343.8) * mm, "radius": 125 * mm});
            skCircle(sketch, "E547.0.0", {"center": v(2776.75, -4864.68) * mm, "radius": 125 * mm});
            skCircle(sketch, "E548.0.0", {"center": v(2716.08, -3866.5) * mm, "radius": 225 * mm, "construction": true});
            skCircle(sketch, "E549.0.0", {"center": v(3234.5, -3362.31) * mm, "radius": 225 * mm, "construction": true});
            skCircle(sketch, "E550.0.0", {"center": v(3772.46, -3883.2) * mm, "radius": 225 * mm, "construction": true});
            skCircle(sketch, "E551.0.0", {"center": v(3254.05, -4387.39) * mm, "radius": 225 * mm, "construction": true});
            skCircle(sketch, "E552.0.0", {"center": v(3711.8, -2885.01) * mm, "radius": 125 * mm});
            skCircle(sketch, "E553.0.0", {"center": v(4189.09, -2407.72) * mm, "radius": 225 * mm, "construction": true});
            skCircle(sketch, "E554.0.0", {"center": v(4249.76, -3405.9) * mm, "radius": 125 * mm});
            skCircle(sketch, "E555.0.0", {"center": v(4727.06, -2928.6) * mm, "radius": 225 * mm, "construction": true});
            skSolve(sketch);
        }
        {
            var Q0;
            Q0 = qSketchRegion(id + "F42", true);
            extrude(context, id + "F43", {"entities" : qUnion([Q0]), "depth" : 50 * mm, "offsetDistance" : 25 * mm});
        }
        {
            var Q0;
            Q0=makeQuery(id+"F43.opExtrude","CAP_FACE",FACE,{"disambiguationData":[OSD([sQuery(id+"F42.wireOp",EDGE,"E546.0.0")])],"isStart":false});
            var sketch = newSketch(context, id + "F44", { "sketchPlane" : qUnion([Q0])});
            skCircle(sketch, "E556.0", {"center": v(2238.78, -4343.8) * mm, "radius": 75 * mm});
            skCircle(sketch, "E557.0", {"center": v(2776.75, -4864.68) * mm, "radius": 75 * mm});
            skCircle(sketch, "E558.0", {"center": v(3711.8, -2885.01) * mm, "radius": 75 * mm});
            skCircle(sketch, "E559.0", {"center": v(4249.76, -3405.9) * mm, "radius": 75 * mm});
            skCircle(sketch, "E560.0", {"center": v(-2012.95, -5020.31) * mm, "radius": 75 * mm});
            skCircle(sketch, "E561.0", {"center": v(-3864.78, -3793.23) * mm, "radius": 75 * mm});
            skCircle(sketch, "E562.0", {"center": v(-3326.8, -3272.34) * mm, "radius": 75 * mm});
            skCircle(sketch, "E563.0", {"center": v(-4597.67, -2047.33) * mm, "radius": 75 * mm});
            skCircle(sketch, "E564.0", {"center": v(-5313.66, -867.26) * mm, "radius": 75 * mm});
            skCircle(sketch, "E565.0", {"center": v(-5313.66, 822.79) * mm, "radius": 75 * mm});
            skCircle(sketch, "E566.0", {"center": v(-5313.66, 0) * mm, "radius": 75 * mm});
            skSolve(sketch);
        }
        {
            var Q0;
            Q0 = qSketchRegion(id + "F44", true);
            extrude(context, id + "F45", {"entities" : qUnion([Q0]), "depth" : 680 * mm, "offsetDistance" : 25 * mm});
        }
        {
            var Q0;
            {var subQ3=sQuery(id+"F0.wireOp",EDGE,"E70");Q0=makeQuery(id+"F0.imprint","IMPRINT",FACE,{"disambiguationData":[TD([[makeQuery(id+"F0.imprint","IMPRINT",EDGE,{"derivedFrom":subQ3}),1.0]])]});}
            var sketch = newSketch(context, id + "F46", { "sketchPlane" : qUnion([Q0])});
            skCircle(sketch, "E567.0", {"center": v(-1289.95, -1284.03) * mm, "radius": 375 * mm});
            skCircle(sketch, "E568.0", {"center": v(1272.05, -1284.03) * mm, "radius": 375 * mm});
            skSolve(sketch);
        }
        {
            var Q0;
            Q0 = qSketchRegion(id + "F46", true);
            extrude(context, id + "F47", {"entities" : qUnion([Q0]), "depth" : 50 * mm, "offsetDistance" : 25 * mm});
        }
        {
            var Q0;
            Q0=makeQuery(id+"F47.opExtrude","CAP_FACE",FACE,{"disambiguationData":[OSD([sQuery(id+"F46.wireOp",EDGE,"E567.0")])],"isStart":false});
            var sketch = newSketch(context, id + "F48", { "sketchPlane" : qUnion([Q0])});
            skCircle(sketch, "E569.0", {"center": v(-1289.95, -1284.03) * mm, "radius": 75 * mm});
            skCircle(sketch, "E570.0", {"center": v(1272.05, -1284.03) * mm, "radius": 75 * mm});
            skSolve(sketch);
        }
        {
            var Q0;
            Q0 = qSketchRegion(id + "F48", true);
            extrude(context, id + "F49", {"entities" : qUnion([Q0]), "depth" : 620 * mm, "offsetDistance" : 25 * mm});
        }
        {
            var Q0;
            Q0=qCreatedBy(makeId("Top.planeOp"),FACE);
            var sketch = newSketch(context, id + "F50", { "sketchPlane" : qUnion([Q0])});
            skLineSegment(sketch, "E571.bottom", {"start": v(-7553.13, 6750) * mm, "end": v(7816.36, 6750) * mm});
            skLineSegment(sketch, "E571.top", {"start": v(-7553.13, -7398.36) * mm, "end": v(7816.36, -7398.36) * mm});
            skLineSegment(sketch, "E571.left", {"start": v(-7553.13, 6750) * mm, "end": v(-7553.13, -7398.36) * mm});
            skLineSegment(sketch, "E571.right", {"start": v(7816.36, 6750) * mm, "end": v(7816.36, -7398.36) * mm});
            skSolve(sketch);
        }
        {
            var Q0;
            Q0 = qSketchRegion(id + "F50", true);
            extrude(context, id + "F51", {"entities" : qUnion([Q0]), "oppositeDirection" : true, "depth" : 25 * mm, "offsetDistance" : 25 * mm});
        }
    });
